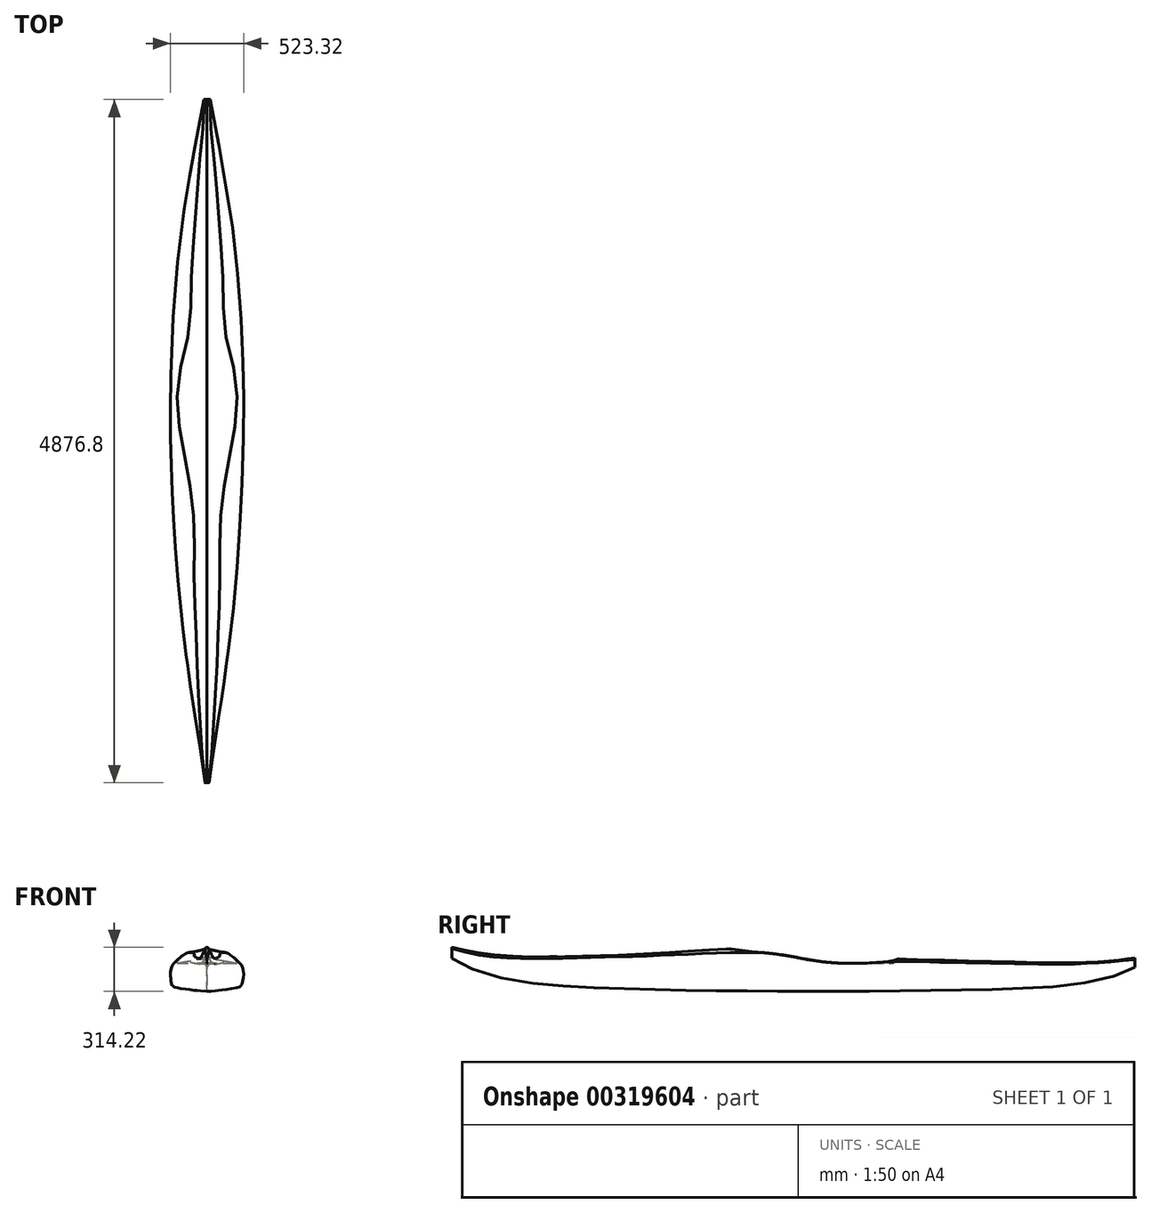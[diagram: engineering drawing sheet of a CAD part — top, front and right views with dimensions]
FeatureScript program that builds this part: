
annotation { "Feature Type Name" : "Feature", "Feature Type Description" : "" }
export const myFeature = defineFeature(function(context is Context, id is Id, definition is map)
    precondition{}
    {
        {
            var Q0;
            Q0=qCreatedBy(makeId("Front.planeOp"),FACE);
            var sketch = newSketch(context, id + "F0", { "sketchPlane" : qUnion([Q0])});
            skLineSegment(sketch, "E0", {"start": v(0, 0) * mm, "end": v(537.15, 0) * mm, "construction": true});
            skPoint(sketch, "E1", {"position": v(0, 0) * mm});
            skLineSegment(sketch, "E2.direction1", {"start": v(0, 0) * mm, "end": v(25.4, 0) * mm, "construction": true});
            skLineSegment(sketch, "E3", {"start": v(0, 0) * mm, "end": v(0, 215.9) * mm, "construction": true});
            skLineSegment(sketch, "E4", {"start": v(25.4, 0) * mm, "end": v(25.4, 210.06) * mm, "construction": true});
            skLineSegment(sketch, "E5", {"start": v(50.8, 0) * mm, "end": v(50.8, 203.7) * mm, "construction": true});
            skLineSegment(sketch, "E6", {"start": v(76.2, 0) * mm, "end": v(76.2, 197.1) * mm, "construction": true});
            skLineSegment(sketch, "E7", {"start": v(101.6, 0) * mm, "end": v(101.6, 190.25) * mm, "construction": true});
            skLineSegment(sketch, "E8", {"start": v(127, 0) * mm, "end": v(127, 181.86) * mm, "construction": true});
            skLineSegment(sketch, "E9", {"start": v(152.4, 0) * mm, "end": v(152.4, 170.43) * mm, "construction": true});
            skLineSegment(sketch, "E10", {"start": v(177.8, 0) * mm, "end": v(177.8, 155.7) * mm, "construction": true});
            skLineSegment(sketch, "E11", {"start": v(203.2, 0) * mm, "end": v(203.2, 136.9) * mm, "construction": true});
            skLineSegment(sketch, "E12", {"start": v(228.6, 0) * mm, "end": v(228.6, 108.97) * mm, "construction": true});
            skLineSegment(sketch, "E13", {"start": v(0, 0) * mm, "end": v(0, -82.55) * mm, "construction": true});
            skLineSegment(sketch, "E14", {"start": v(25.4, 0) * mm, "end": v(25.4, -79.76) * mm, "construction": true});
            skLineSegment(sketch, "E15", {"start": v(50.8, 0) * mm, "end": v(50.8, -76.7) * mm, "construction": true});
            skLineSegment(sketch, "E16", {"start": v(76.2, 0) * mm, "end": v(76.2, -73.15) * mm, "construction": true});
            skLineSegment(sketch, "E17", {"start": v(101.6, 0) * mm, "end": v(101.6, -69.34) * mm, "construction": true});
            skLineSegment(sketch, "E18", {"start": v(127, 0) * mm, "end": v(127, -65.02) * mm, "construction": true});
            skLineSegment(sketch, "E19", {"start": v(152.4, 0) * mm, "end": v(152.4, -59.44) * mm, "construction": true});
            skLineSegment(sketch, "E20", {"start": v(177.8, 0) * mm, "end": v(177.8, -53.09) * mm, "construction": true});
            skLineSegment(sketch, "E21", {"start": v(203.2, 0) * mm, "end": v(203.2, -43.43) * mm, "construction": true});
            skLineSegment(sketch, "E22", {"start": v(228.6, 0) * mm, "end": v(228.6, -24.13) * mm, "construction": true});
            skPoint(sketch, "E23.0.1.0", {"position": v(0, 25.4) * mm});
            skPoint(sketch, "E23.0.2.0", {"position": v(0, 50.8) * mm});
            skPoint(sketch, "E23.0.3.0", {"position": v(0, 76.2) * mm});
            skPoint(sketch, "E23.0.4.0", {"position": v(0, 101.6) * mm});
            skPoint(sketch, "E23.0.5.0", {"position": v(0, 127) * mm});
            skPoint(sketch, "E23.0.6.0", {"position": v(0, 152.4) * mm});
            skLineSegment(sketch, "E23.direction2", {"start": v(0, 0) * mm, "end": v(0, 25.4) * mm, "construction": true});
            skLineSegment(sketch, "E24", {"start": v(0, 25.4) * mm, "end": v(241.8, 25.4) * mm, "construction": true});
            skLineSegment(sketch, "E25", {"start": v(0, 50.8) * mm, "end": v(243.33, 50.8) * mm, "construction": true});
            skLineSegment(sketch, "E26", {"start": v(0, 76.2) * mm, "end": v(241.3, 76.2) * mm, "construction": true});
            skLineSegment(sketch, "E27", {"start": v(0, 101.6) * mm, "end": v(232.92, 101.6) * mm, "construction": true});
            skPoint(sketch, "E28", {"position": v(238, 0) * mm});
            skFitSpline(sketch, "E29", {"points": [v(0, 215.9) * mm, v(25.4, 210.06) * mm, v(50.8, 203.7) * mm, v(76.2, 197.1) * mm, v(101.6, 190.25) * mm, v(127, 181.86) * mm, v(152.4, 170.43) * mm, v(177.8, 155.7) * mm, v(203.2, 136.9) * mm, v(228.6, 108.97) * mm, v(241.3, 76.2) * mm, v(243.33, 50.8) * mm, v(241.8, 25.4) * mm, v(238, 0) * mm, v(228.6, -24.13) * mm, v(203.2, -43.43) * mm, v(177.8, -53.09) * mm, v(152.4, -59.44) * mm, v(127, -65.02) * mm, v(101.6, -69.34) * mm, v(76.2, -73.15) * mm, v(50.8, -76.7) * mm, v(25.4, -79.76) * mm, v(0, -82.55) * mm], "startDerivative": vector(600.69, -135.37) * mm, "endDerivative": vector(-606.38, -65.85) * mm});
            skFitSpline(sketch, "E30.MirrorCS", {"points": [v(0, 215.9) * mm, v(-25.4, 210.06) * mm, v(-50.8, 203.7) * mm, v(-76.2, 197.1) * mm, v(-101.6, 190.25) * mm, v(-127, 181.86) * mm, v(-152.4, 170.43) * mm, v(-177.8, 155.7) * mm, v(-203.2, 136.9) * mm, v(-228.6, 108.97) * mm, v(-241.3, 76.2) * mm, v(-243.33, 50.8) * mm, v(-241.8, 25.4) * mm, v(-238, 0) * mm, v(-228.6, -24.13) * mm, v(-203.2, -43.43) * mm, v(-177.8, -53.09) * mm, v(-152.4, -59.44) * mm, v(-127, -65.02) * mm, v(-101.6, -69.34) * mm, v(-76.2, -73.15) * mm, v(-50.8, -76.7) * mm, v(-25.4, -79.76) * mm, v(0, -82.55) * mm], "startDerivative": vector(-600.69, -135.37) * mm, "endDerivative": vector(606.38, -65.85) * mm});
            skPoint(sketch, "E31.0.0.7", {"position": v(0, 177.8) * mm});
            skPoint(sketch, "E32.0.0.8", {"position": v(0, 203.2) * mm});
            skPoint(sketch, "E33.0.1.0", {"position": v(25.4, 0) * mm});
            skPoint(sketch, "E33.0.2.0", {"position": v(50.8, 0) * mm});
            skPoint(sketch, "E33.0.3.0", {"position": v(76.2, 0) * mm});
            skPoint(sketch, "E33.0.4.0", {"position": v(101.6, 0) * mm});
            skPoint(sketch, "E33.0.5.0", {"position": v(127, 0) * mm});
            skPoint(sketch, "E33.0.6.0", {"position": v(152.4, 0) * mm});
            skPoint(sketch, "E33.0.7.0", {"position": v(177.8, 0) * mm});
            skPoint(sketch, "E33.0.8.0", {"position": v(203.2, 0) * mm});
            skPoint(sketch, "E33.0.9.0", {"position": v(228.6, 0) * mm});
            skPoint(sketch, "E34.0.10.0", {"position": v(254, 0) * mm});
            skPoint(sketch, "E35.0.11.0", {"position": v(279.4, 0) * mm});
            skPoint(sketch, "E36", {"position": v(0, -25.4) * mm});
            skPoint(sketch, "E37", {"position": v(0, -50.8) * mm});
            skPoint(sketch, "E38", {"position": v(0, -76.2) * mm});
            skLineSegment(sketch, "E39", {"start": v(0, -82.55) * mm, "end": v(0, 215.9) * mm});
            skLineSegment(sketch, "E40", {"start": v(0, 215.9) * mm, "end": v(0, -82.55) * mm});
            skSolve(sketch);
        }
        {
            var Q0;
            Q0=makeQuery(id+"F0.imprint","IMPRINT",FACE,{"disambiguationData":[TD([[makeQuery(id+"F0.imprint","IMPRINT",EDGE,{"derivedFrom":sQuery(id+"F0.wireOp",EDGE,"E29")}),-1.0]])]});
            cPlane(context, id + "F1", {"entities" : qUnion([Q0]), "cplaneType" : CPlaneType.OFFSET, "offset" : 304.8 * mm, "width" : 152.4 * mm, "height" : 152.4 * mm});
        }
        {
            var Q0;
            Q0=qCreatedBy(id+"F1.planeOp",FACE);
            var sketch = newSketch(context, id + "F2", { "sketchPlane" : qUnion([Q0])});
            skPoint(sketch, "E41.0", {"position": v(0, 0) * mm});
            skPoint(sketch, "E42.0", {"position": v(25.4, 0) * mm});
            skPoint(sketch, "E43.0", {"position": v(50.8, 0) * mm});
            skPoint(sketch, "E44.0", {"position": v(76.2, 0) * mm});
            skPoint(sketch, "E45.0", {"position": v(101.6, 0) * mm});
            skPoint(sketch, "E46.0", {"position": v(127, 0) * mm});
            skPoint(sketch, "E47.0", {"position": v(177.8, 0) * mm});
            skPoint(sketch, "E48.0", {"position": v(203.2, 0) * mm});
            skPoint(sketch, "E49.0", {"position": v(0, 25.4) * mm});
            skPoint(sketch, "E50.0", {"position": v(0, 50.8) * mm});
            skPoint(sketch, "E51.0", {"position": v(0, 76.2) * mm});
            skPoint(sketch, "E52.0", {"position": v(0, 101.6) * mm});
            skPoint(sketch, "E53.0", {"position": v(152.4, 0) * mm});
            skLineSegment(sketch, "E54", {"start": v(0, 0) * mm, "end": v(0, 198.12) * mm, "construction": true});
            skLineSegment(sketch, "E55", {"start": v(25.4, 0) * mm, "end": v(25.4, 192.53) * mm, "construction": true});
            skLineSegment(sketch, "E56", {"start": v(50.8, 0) * mm, "end": v(50.8, 187.2) * mm, "construction": true});
            skLineSegment(sketch, "E57", {"start": v(76.2, 0) * mm, "end": v(76.2, 181.61) * mm, "construction": true});
            skLineSegment(sketch, "E58", {"start": v(101.6, 0) * mm, "end": v(101.6, 175.51) * mm, "construction": true});
            skLineSegment(sketch, "E59", {"start": v(127, 0) * mm, "end": v(127, 167.9) * mm, "construction": true});
            skLineSegment(sketch, "E60", {"start": v(152.4, 0) * mm, "end": v(152.4, 157.23) * mm, "construction": true});
            skLineSegment(sketch, "E61", {"start": v(177.8, 0) * mm, "end": v(177.8, 142.75) * mm, "construction": true});
            skLineSegment(sketch, "E62", {"start": v(203.2, 0) * mm, "end": v(203.2, 120.65) * mm, "construction": true});
            skLineSegment(sketch, "E63", {"start": v(0, 0) * mm, "end": v(0, -78.23) * mm, "construction": true});
            skLineSegment(sketch, "E64", {"start": v(25.4, 0) * mm, "end": v(25.4, -73.91) * mm, "construction": true});
            skLineSegment(sketch, "E65", {"start": v(50.8, 0) * mm, "end": v(50.8, -69.34) * mm, "construction": true});
            skLineSegment(sketch, "E66", {"start": v(76.2, 0) * mm, "end": v(76.2, -64.52) * mm, "construction": true});
            skLineSegment(sketch, "E67", {"start": v(101.6, 0) * mm, "end": v(101.6, -58.93) * mm, "construction": true});
            skLineSegment(sketch, "E68", {"start": v(127, 0) * mm, "end": v(127, -52.83) * mm, "construction": true});
            skLineSegment(sketch, "E69", {"start": v(152.4, 0) * mm, "end": v(152.4, -45.72) * mm, "construction": true});
            skLineSegment(sketch, "E70", {"start": v(177.8, 0) * mm, "end": v(177.8, -36.32) * mm, "construction": true});
            skLineSegment(sketch, "E71", {"start": v(203.2, 0) * mm, "end": v(203.2, -20.83) * mm, "construction": true});
            skLineSegment(sketch, "E72", {"start": v(0, 25.4) * mm, "end": v(222.5, 25.4) * mm, "construction": true});
            skLineSegment(sketch, "E73", {"start": v(0, 50.8) * mm, "end": v(225.04, 50.8) * mm, "construction": true});
            skLineSegment(sketch, "E74", {"start": v(0, 0) * mm, "end": v(215.9, 0) * mm, "construction": true});
            skLineSegment(sketch, "E75", {"start": v(0, 76.2) * mm, "end": v(223.77, 76.2) * mm, "construction": true});
            skLineSegment(sketch, "E76", {"start": v(0, 101.6) * mm, "end": v(216.4, 101.6) * mm, "construction": true});
            skFitSpline(sketch, "E77", {"points": [v(0, 198.12) * mm, v(25.4, 192.53) * mm, v(50.8, 187.2) * mm, v(76.2, 181.61) * mm, v(101.6, 175.51) * mm, v(127, 167.9) * mm, v(152.4, 157.23) * mm, v(177.8, 142.75) * mm, v(203.2, 120.65) * mm, v(216.4, 101.6) * mm, v(223.77, 76.2) * mm, v(225.04, 50.8) * mm, v(222.5, 25.4) * mm, v(215.9, 0) * mm, v(203.2, -20.83) * mm, v(177.8, -36.32) * mm, v(152.4, -45.72) * mm, v(127, -52.83) * mm, v(101.6, -58.93) * mm, v(76.2, -64.52) * mm, v(50.8, -69.34) * mm, v(25.4, -73.91) * mm, v(0, -78.23) * mm], "startDerivative": vector(564.48, -125.99) * mm, "endDerivative": vector(-567.44, -95.07) * mm});
            skFitSpline(sketch, "E78.MirrorCS", {"points": [v(0, 198.12) * mm, v(-25.4, 192.53) * mm, v(-50.8, 187.2) * mm, v(-76.2, 181.61) * mm, v(-101.6, 175.51) * mm, v(-127, 167.9) * mm, v(-152.4, 157.23) * mm, v(-177.8, 142.75) * mm, v(-203.2, 120.65) * mm, v(-216.4, 101.6) * mm, v(-223.77, 76.2) * mm, v(-225.04, 50.8) * mm, v(-222.5, 25.4) * mm, v(-215.9, 0) * mm, v(-203.2, -20.83) * mm, v(-177.8, -36.32) * mm, v(-152.4, -45.72) * mm, v(-127, -52.83) * mm, v(-101.6, -58.93) * mm, v(-76.2, -64.52) * mm, v(-50.8, -69.34) * mm, v(-25.4, -73.91) * mm, v(0, -78.23) * mm], "startDerivative": vector(-564.48, -125.99) * mm, "endDerivative": vector(567.44, -95.07) * mm});
            skLineSegment(sketch, "E79", {"start": v(0, 198.12) * mm, "end": v(0, -78.23) * mm});
            skSolve(sketch);
        }
        {
            var Q0;
            Q0=makeQuery(id+"F2.imprint","IMPRINT",FACE,{"disambiguationData":[TD([[makeQuery(id+"F2.imprint","IMPRINT",EDGE,{"derivedFrom":sQuery(id+"F2.wireOp",EDGE,"E77")}),-1.0]])]});
            cPlane(context, id + "F3", {"entities" : qUnion([Q0]), "cplaneType" : CPlaneType.OFFSET, "offset" : 304.8 * mm, "width" : 152.4 * mm, "height" : 152.4 * mm});
        }
        {
            var Q0;
            Q0=qCreatedBy(id+"F3.planeOp",FACE);
            var sketch = newSketch(context, id + "F4", { "sketchPlane" : qUnion([Q0])});
            skPoint(sketch, "E80.0", {"position": v(0, 0) * mm});
            skPoint(sketch, "E81.0", {"position": v(25.4, 0) * mm});
            skPoint(sketch, "E82.0", {"position": v(50.8, 0) * mm});
            skPoint(sketch, "E83.0", {"position": v(76.2, 0) * mm});
            skPoint(sketch, "E84.0", {"position": v(101.6, 0) * mm});
            skPoint(sketch, "E85.0", {"position": v(127, 0) * mm});
            skPoint(sketch, "E86.0", {"position": v(152.4, 0) * mm});
            skPoint(sketch, "E87.0", {"position": v(177.8, 0) * mm});
            skPoint(sketch, "E88.0", {"position": v(0, 25.4) * mm});
            skPoint(sketch, "E89.0", {"position": v(0, 50.8) * mm});
            skPoint(sketch, "E90.0", {"position": v(0, 76.2) * mm});
            skPoint(sketch, "E91.0", {"position": v(0, 101.6) * mm});
            skLineSegment(sketch, "E92", {"start": v(0, 0) * mm, "end": v(0, 181.36) * mm, "construction": true});
            skLineSegment(sketch, "E93", {"start": v(25.4, 0) * mm, "end": v(25.4, 177.3) * mm, "construction": true});
            skLineSegment(sketch, "E94", {"start": v(50.8, 0) * mm, "end": v(50.8, 172.97) * mm, "construction": true});
            skLineSegment(sketch, "E95", {"start": v(76.2, 0) * mm, "end": v(76.2, 168.66) * mm, "construction": true});
            skLineSegment(sketch, "E96", {"start": v(101.6, 0) * mm, "end": v(101.6, 163.07) * mm, "construction": true});
            skLineSegment(sketch, "E97", {"start": v(127, 0) * mm, "end": v(127, 154.94) * mm, "construction": true});
            skLineSegment(sketch, "E98", {"start": v(152.4, 0) * mm, "end": v(152.4, 142.5) * mm, "construction": true});
            skLineSegment(sketch, "E99", {"start": v(177.8, 0) * mm, "end": v(177.8, 123.2) * mm, "construction": true});
            skLineSegment(sketch, "E100", {"start": v(0, 0) * mm, "end": v(0, -72.14) * mm, "construction": true});
            skLineSegment(sketch, "E101", {"start": v(25.4, 0) * mm, "end": v(25.4, -65.02) * mm, "construction": true});
            skLineSegment(sketch, "E102", {"start": v(50.8, 0) * mm, "end": v(50.8, -58.17) * mm, "construction": true});
            skLineSegment(sketch, "E103", {"start": v(76.2, 0) * mm, "end": v(76.2, -50.8) * mm, "construction": true});
            skLineSegment(sketch, "E104", {"start": v(101.6, 0) * mm, "end": v(101.6, -42.93) * mm, "construction": true});
            skLineSegment(sketch, "E105", {"start": v(127, 0) * mm, "end": v(127, -34.04) * mm, "construction": true});
            skLineSegment(sketch, "E106", {"start": v(152.4, 0) * mm, "end": v(152.4, -23.37) * mm, "construction": true});
            skLineSegment(sketch, "E107", {"start": v(177.8, 0) * mm, "end": v(177.8, -7.37) * mm, "construction": true});
            skLineSegment(sketch, "E108", {"start": v(0, 0) * mm, "end": v(184.66, 0) * mm, "construction": true});
            skLineSegment(sketch, "E109", {"start": v(0, 25.4) * mm, "end": v(195.58, 25.4) * mm, "construction": true});
            skLineSegment(sketch, "E110", {"start": v(0, 50.8) * mm, "end": v(200.15, 50.8) * mm, "construction": true});
            skLineSegment(sketch, "E111", {"start": v(0, 76.2) * mm, "end": v(199.9, 76.2) * mm, "construction": true});
            skLineSegment(sketch, "E112", {"start": v(0, 101.6) * mm, "end": v(193.3, 101.6) * mm, "construction": true});
            skFitSpline(sketch, "E113", {"points": [v(0, 181.36) * mm, v(25.4, 177.3) * mm, v(50.8, 172.97) * mm, v(76.2, 168.66) * mm, v(101.6, 163.07) * mm, v(127, 154.94) * mm, v(152.4, 142.5) * mm, v(177.8, 123.2) * mm, v(193.3, 101.6) * mm, v(199.9, 76.2) * mm, v(200.15, 50.8) * mm, v(195.58, 25.4) * mm, v(184.66, 0) * mm, v(177.8, -7.37) * mm, v(152.4, -23.37) * mm, v(127, -34.04) * mm, v(101.6, -42.93) * mm, v(76.2, -50.8) * mm, v(50.8, -58.17) * mm, v(25.4, -65.02) * mm, v(0, -72.14) * mm], "startDerivative": vector(509.78, -79.9) * mm, "endDerivative": vector(-503.06, -142.83) * mm});
            skFitSpline(sketch, "E114.MirrorCS", {"points": [v(0, 181.36) * mm, v(-25.4, 177.3) * mm, v(-50.8, 172.97) * mm, v(-76.2, 168.66) * mm, v(-101.6, 163.07) * mm, v(-127, 154.94) * mm, v(-152.4, 142.5) * mm, v(-177.8, 123.2) * mm, v(-193.3, 101.6) * mm, v(-199.9, 76.2) * mm, v(-200.15, 50.8) * mm, v(-195.58, 25.4) * mm, v(-184.66, 0) * mm, v(-177.8, -7.37) * mm, v(-152.4, -23.37) * mm, v(-127, -34.04) * mm, v(-101.6, -42.93) * mm, v(-76.2, -50.8) * mm, v(-50.8, -58.17) * mm, v(-25.4, -65.02) * mm, v(0, -72.14) * mm], "startDerivative": vector(-509.78, -79.9) * mm, "endDerivative": vector(503.06, -142.83) * mm});
            skLineSegment(sketch, "E115", {"start": v(0, 181.36) * mm, "end": v(0, -72.14) * mm});
            skSolve(sketch);
        }
        {
            var Q0;
            Q0=makeQuery(id+"F4.imprint","IMPRINT",FACE,{"disambiguationData":[TD([[makeQuery(id+"F4.imprint","IMPRINT",EDGE,{"derivedFrom":sQuery(id+"F4.wireOp",EDGE,"E113")}),-1.0]])]});
            cPlane(context, id + "F5", {"entities" : qUnion([Q0]), "cplaneType" : CPlaneType.OFFSET, "offset" : 304.8 * mm, "width" : 152.4 * mm, "height" : 152.4 * mm});
        }
        {
            var Q0;
            Q0=qCreatedBy(id+"F5.planeOp",FACE);
            var sketch = newSketch(context, id + "F6", { "sketchPlane" : qUnion([Q0])});
            skPoint(sketch, "E116.0", {"position": v(0, 0) * mm});
            skPoint(sketch, "E117.0", {"position": v(25.4, 0) * mm});
            skPoint(sketch, "E118.0", {"position": v(50.8, 0) * mm});
            skPoint(sketch, "E119.0", {"position": v(76.2, 0) * mm});
            skPoint(sketch, "E120.0", {"position": v(101.6, 0) * mm});
            skPoint(sketch, "E121.0", {"position": v(127, 0) * mm});
            skPoint(sketch, "E122.0", {"position": v(152.4, 0) * mm});
            skPoint(sketch, "E123.0", {"position": v(0, 25.4) * mm});
            skPoint(sketch, "E124.0", {"position": v(0, 50.8) * mm});
            skPoint(sketch, "E125.0", {"position": v(0, 76.2) * mm});
            skPoint(sketch, "E126.0", {"position": v(0, 101.6) * mm});
            skPoint(sketch, "E127.0", {"position": v(0, 127) * mm});
            skPoint(sketch, "E128.0", {"position": v(0, 152.4) * mm});
            skLineSegment(sketch, "E129", {"start": v(0, 0) * mm, "end": v(0, 168.15) * mm, "construction": true});
            skLineSegment(sketch, "E130", {"start": v(25.4, 0) * mm, "end": v(25.4, 165.6) * mm, "construction": true});
            skLineSegment(sketch, "E131", {"start": v(50.8, 0) * mm, "end": v(50.8, 162.3) * mm, "construction": true});
            skLineSegment(sketch, "E132", {"start": v(76.2, 0) * mm, "end": v(76.2, 157.99) * mm, "construction": true});
            skLineSegment(sketch, "E133", {"start": v(101.6, 0) * mm, "end": v(101.6, 150.62) * mm, "construction": true});
            skLineSegment(sketch, "E134", {"start": v(127, 0) * mm, "end": v(127, 138.68) * mm, "construction": true});
            skLineSegment(sketch, "E135", {"start": v(152.4, 0) * mm, "end": v(152.4, 118.11) * mm, "construction": true});
            skLineSegment(sketch, "E136", {"start": v(0, 0) * mm, "end": v(0, -61.47) * mm, "construction": true});
            skLineSegment(sketch, "E137", {"start": v(25.4, 0) * mm, "end": v(25.4, -50.3) * mm, "construction": true});
            skLineSegment(sketch, "E138", {"start": v(50.8, 0) * mm, "end": v(50.8, -40.13) * mm, "construction": true});
            skLineSegment(sketch, "E139", {"start": v(76.2, 0) * mm, "end": v(76.2, -29.46) * mm, "construction": true});
            skLineSegment(sketch, "E140", {"start": v(101.6, 0) * mm, "end": v(101.6, -18.03) * mm, "construction": true});
            skLineSegment(sketch, "E141", {"start": v(127, 0) * mm, "end": v(127, -4.57) * mm, "construction": true});
            skLineSegment(sketch, "E142", {"start": v(0, 0) * mm, "end": v(134.37, 0) * mm, "construction": true});
            skLineSegment(sketch, "E143", {"start": v(0, 25.4) * mm, "end": v(158.5, 25.4) * mm, "construction": true});
            skLineSegment(sketch, "E144", {"start": v(0, 50.8) * mm, "end": v(166.62, 50.8) * mm, "construction": true});
            skLineSegment(sketch, "E145", {"start": v(0, 76.2) * mm, "end": v(168.4, 76.2) * mm, "construction": true});
            skLineSegment(sketch, "E146", {"start": v(0, 101.6) * mm, "end": v(162.56, 101.6) * mm, "construction": true});
            skPoint(sketch, "E147", {"position": v(152.4, 15.5) * mm});
            skFitSpline(sketch, "E148", {"points": [v(0, 168.15) * mm, v(25.4, 165.6) * mm, v(50.8, 162.3) * mm, v(76.2, 157.99) * mm, v(101.6, 150.62) * mm, v(127, 138.68) * mm, v(152.4, 118.11) * mm, v(162.56, 101.6) * mm, v(168.4, 76.2) * mm, v(166.62, 50.8) * mm, v(158.5, 25.4) * mm, v(152.4, 15.5) * mm, v(134.37, 0) * mm, v(127, -4.57) * mm, v(101.6, -18.03) * mm, v(76.2, -29.46) * mm, v(50.8, -40.13) * mm, v(25.4, -50.3) * mm, v(0, -61.47) * mm], "startDerivative": vector(445.96, -41.5) * mm, "endDerivative": vector(-427.08, -193.13) * mm});
            skFitSpline(sketch, "E149.MirrorCS", {"points": [v(0, 168.15) * mm, v(-25.4, 165.6) * mm, v(-50.8, 162.3) * mm, v(-76.2, 157.99) * mm, v(-101.6, 150.62) * mm, v(-127, 138.68) * mm, v(-152.4, 118.11) * mm, v(-162.56, 101.6) * mm, v(-168.4, 76.2) * mm, v(-166.62, 50.8) * mm, v(-158.5, 25.4) * mm, v(-152.4, 15.5) * mm, v(-134.37, 0) * mm, v(-127, -4.57) * mm, v(-101.6, -18.03) * mm, v(-76.2, -29.46) * mm, v(-50.8, -40.13) * mm, v(-25.4, -50.3) * mm, v(0, -61.47) * mm], "startDerivative": vector(-445.96, -41.5) * mm, "endDerivative": vector(427.08, -193.13) * mm});
            skLineSegment(sketch, "E150", {"start": v(0, 168.15) * mm, "end": v(0, -61.47) * mm});
            skSolve(sketch);
        }
        {
            var Q0;
            Q0=makeQuery(id+"F6.imprint","IMPRINT",FACE,{"disambiguationData":[TD([[makeQuery(id+"F6.imprint","IMPRINT",EDGE,{"derivedFrom":sQuery(id+"F6.wireOp",EDGE,"E148")}),-1.0]])]});
            cPlane(context, id + "F7", {"entities" : qUnion([Q0]), "cplaneType" : CPlaneType.OFFSET, "offset" : 304.8 * mm, "width" : 152.4 * mm, "height" : 152.4 * mm});
        }
        {
            var Q0;
            Q0=qCreatedBy(id+"F7.planeOp",FACE);
            var sketch = newSketch(context, id + "F8", { "sketchPlane" : qUnion([Q0])});
            skPoint(sketch, "E151.0", {"position": v(0, 0) * mm});
            skPoint(sketch, "E152.0", {"position": v(25.4, 0) * mm});
            skPoint(sketch, "E153.0", {"position": v(50.8, 0) * mm});
            skPoint(sketch, "E154.0", {"position": v(76.2, 0) * mm});
            skPoint(sketch, "E155.0", {"position": v(101.6, 0) * mm});
            skPoint(sketch, "E156.0", {"position": v(127, 0) * mm});
            skPoint(sketch, "E157.0", {"position": v(0, 25.4) * mm});
            skPoint(sketch, "E158.0", {"position": v(0, 50.8) * mm});
            skPoint(sketch, "E159.0", {"position": v(0, 76.2) * mm});
            skPoint(sketch, "E160.0", {"position": v(0, 101.6) * mm});
            skLineSegment(sketch, "E161", {"start": v(0, 0) * mm, "end": v(0, 161.3) * mm, "construction": true});
            skLineSegment(sketch, "E162", {"start": v(25.4, 0) * mm, "end": v(25.4, 159.51) * mm, "construction": true});
            skLineSegment(sketch, "E163", {"start": v(50.8, 0) * mm, "end": v(50.8, 155.2) * mm, "construction": true});
            skLineSegment(sketch, "E164", {"start": v(76.2, 0) * mm, "end": v(76.2, 147.07) * mm, "construction": true});
            skLineSegment(sketch, "E165", {"start": v(101.6, 0) * mm, "end": v(101.6, 132.84) * mm, "construction": true});
            skLineSegment(sketch, "E166", {"start": v(127, 0) * mm, "end": v(127, 96.27) * mm, "construction": true});
            skLineSegment(sketch, "E167", {"start": v(0, 0) * mm, "end": v(0, -44.2) * mm, "construction": true});
            skLineSegment(sketch, "E168", {"start": v(25.4, 0) * mm, "end": v(25.4, -27.43) * mm, "construction": true});
            skLineSegment(sketch, "E169", {"start": v(50.8, 0) * mm, "end": v(50.8, -12.45) * mm, "construction": true});
            skLineSegment(sketch, "E170", {"start": v(76.2, 0) * mm, "end": v(76.2, 3.81) * mm, "construction": true});
            skLineSegment(sketch, "E171", {"start": v(101.6, 0) * mm, "end": v(101.6, 22.35) * mm, "construction": true});
            skLineSegment(sketch, "E172", {"start": v(127, 0) * mm, "end": v(127, 65.02) * mm, "construction": true});
            skLineSegment(sketch, "E173", {"start": v(0, 76.2) * mm, "end": v(128.52, 76.2) * mm, "construction": true});
            skLineSegment(sketch, "E174", {"start": v(0, 50.8) * mm, "end": v(122.94, 50.8) * mm, "construction": true});
            skLineSegment(sketch, "E175", {"start": v(0, 25.4) * mm, "end": v(104.9, 25.4) * mm, "construction": true});
            skLineSegment(sketch, "E176", {"start": v(0, 0) * mm, "end": v(70.36, 0) * mm, "construction": true});
            skPoint(sketch, "E177", {"position": v(0, -25.4) * mm});
            skFitSpline(sketch, "E178", {"points": [v(0, 161.3) * mm, v(25.4, 159.51) * mm, v(50.8, 155.2) * mm, v(76.2, 147.07) * mm, v(101.6, 132.84) * mm, v(127, 96.27) * mm, v(128.52, 76.2) * mm, v(127, 65.02) * mm, v(122.94, 50.8) * mm, v(104.9, 25.4) * mm, v(101.6, 22.35) * mm, v(76.2, 3.81) * mm, v(70.36, 0) * mm, v(50.8, -12.45) * mm, v(25.4, -27.43) * mm, v(0, -44.2) * mm], "startDerivative": vector(393.47, -0.46) * mm, "endDerivative": vector(-325.6, -222.45) * mm});
            skFitSpline(sketch, "E179.MirrorCS", {"points": [v(0, 161.3) * mm, v(-25.4, 159.51) * mm, v(-50.8, 155.2) * mm, v(-76.2, 147.07) * mm, v(-101.6, 132.84) * mm, v(-127, 96.27) * mm, v(-128.52, 76.2) * mm, v(-127, 65.02) * mm, v(-122.94, 50.8) * mm, v(-104.9, 25.4) * mm, v(-101.6, 22.35) * mm, v(-76.2, 3.81) * mm, v(-70.36, 0) * mm, v(-50.8, -12.45) * mm, v(-25.4, -27.43) * mm, v(0, -44.2) * mm], "startDerivative": vector(-393.47, -0.46) * mm, "endDerivative": vector(325.6, -222.45) * mm});
            skLineSegment(sketch, "E180", {"start": v(0, 161.3) * mm, "end": v(0, -44.2) * mm});
            skSolve(sketch);
        }
        {
            var Q0;
            Q0=makeQuery(id+"F8.imprint","IMPRINT",FACE,{"disambiguationData":[TD([[makeQuery(id+"F8.imprint","IMPRINT",EDGE,{"derivedFrom":sQuery(id+"F8.wireOp",EDGE,"E178")}),-1.0]])]});
            cPlane(context, id + "F9", {"entities" : qUnion([Q0]), "cplaneType" : CPlaneType.OFFSET, "offset" : 304.8 * mm, "width" : 152.4 * mm, "height" : 152.4 * mm});
        }
        {
            var Q0;
            Q0=qCreatedBy(id+"F9.planeOp",FACE);
            var sketch = newSketch(context, id + "F10", { "sketchPlane" : qUnion([Q0])});
            skPoint(sketch, "E181.0", {"position": v(0, 0) * mm});
            skPoint(sketch, "E182.0", {"position": v(25.4, 0) * mm});
            skPoint(sketch, "E183.0", {"position": v(50.8, 0) * mm});
            skPoint(sketch, "E184.0", {"position": v(76.2, 0) * mm});
            skPoint(sketch, "E185.0", {"position": v(0, 25.4) * mm});
            skPoint(sketch, "E186.0", {"position": v(0, 50.8) * mm});
            skPoint(sketch, "E187.0", {"position": v(0, 76.2) * mm});
            skPoint(sketch, "E188.0", {"position": v(0, 101.6) * mm});
            skPoint(sketch, "E189.0", {"position": v(0, 127) * mm});
            skPoint(sketch, "E190.0", {"position": v(0, 152.4) * mm});
            skLineSegment(sketch, "E191", {"start": v(0, 0) * mm, "end": v(0, 163.58) * mm, "construction": true});
            skLineSegment(sketch, "E192", {"start": v(25.4, 0) * mm, "end": v(25.4, 160.27) * mm, "construction": true});
            skLineSegment(sketch, "E193", {"start": v(50.8, 0) * mm, "end": v(50.8, 148.84) * mm, "construction": true});
            skLineSegment(sketch, "E194", {"start": v(76.2, 0) * mm, "end": v(76.2, 123.95) * mm, "construction": true});
            skLineSegment(sketch, "E195", {"start": v(0, 0) * mm, "end": v(0, -10.41) * mm, "construction": true});
            skLineSegment(sketch, "E196", {"start": v(25.4, 0) * mm, "end": v(25.4, 12.95) * mm, "construction": true});
            skLineSegment(sketch, "E197", {"start": v(50.8, 0) * mm, "end": v(50.8, 39.62) * mm, "construction": true});
            skLineSegment(sketch, "E198", {"start": v(76.2, 0) * mm, "end": v(76.2, 73.91) * mm, "construction": true});
            skLineSegment(sketch, "E199", {"start": v(0, 101.6) * mm, "end": v(81.79, 101.6) * mm, "construction": true});
            skLineSegment(sketch, "E200", {"start": v(0, 76.2) * mm, "end": v(77.22, 76.2) * mm, "construction": true});
            skLineSegment(sketch, "E201", {"start": v(0, 50.8) * mm, "end": v(60.96, 50.8) * mm, "construction": true});
            skLineSegment(sketch, "E202", {"start": v(0, 25.4) * mm, "end": v(37.85, 25.4) * mm, "construction": true});
            skLineSegment(sketch, "E203", {"start": v(0, 0) * mm, "end": v(12.2, 0) * mm, "construction": true});
            skLineSegment(sketch, "E204", {"start": v(0, 152.4) * mm, "end": v(44.96, 152.4) * mm, "construction": true});
            skFitSpline(sketch, "E205", {"points": [v(0, 163.58) * mm, v(25.4, 160.27) * mm, v(44.96, 152.4) * mm, v(50.8, 148.84) * mm, v(76.2, 123.95) * mm, v(81.79, 101.6) * mm, v(77.22, 76.2) * mm, v(60.96, 50.8) * mm, v(50.8, 39.62) * mm, v(37.85, 25.4) * mm, v(25.4, 12.95) * mm, v(12.2, 0) * mm, v(0, -10.41) * mm], "startDerivative": vector(320.67, -11.88) * mm, "endDerivative": vector(-169.53, -138.95) * mm});
            skFitSpline(sketch, "E206.MirrorCS", {"points": [v(0, 163.58) * mm, v(-25.4, 160.27) * mm, v(-44.96, 152.4) * mm, v(-50.8, 148.84) * mm, v(-76.2, 123.95) * mm, v(-81.79, 101.6) * mm, v(-77.22, 76.2) * mm, v(-60.96, 50.8) * mm, v(-50.8, 39.62) * mm, v(-37.85, 25.4) * mm, v(-25.4, 12.95) * mm, v(-12.2, 0) * mm, v(0, -10.41) * mm], "startDerivative": vector(-320.67, -11.88) * mm, "endDerivative": vector(169.53, -138.95) * mm});
            skLineSegment(sketch, "E207", {"start": v(0, 163.58) * mm, "end": v(0, -10.41) * mm});
            skSolve(sketch);
        }
        {
            var Q0;
            Q0=makeQuery(id+"F10.imprint","IMPRINT",FACE,{"disambiguationData":[TD([[makeQuery(id+"F10.imprint","IMPRINT",EDGE,{"derivedFrom":sQuery(id+"F10.wireOp",EDGE,"E205")}),-1.0]])]});
            cPlane(context, id + "F11", {"entities" : qUnion([Q0]), "cplaneType" : CPlaneType.OFFSET, "offset" : 304.8 * mm, "width" : 152.4 * mm, "height" : 152.4 * mm});
        }
        {
            var Q0;
            Q0=qCreatedBy(id+"F11.planeOp",FACE);
            var sketch = newSketch(context, id + "F12", { "sketchPlane" : qUnion([Q0])});
            skPoint(sketch, "E208.0", {"position": v(0, 0) * mm});
            skPoint(sketch, "E209.0", {"position": v(25.4, 0) * mm});
            skPoint(sketch, "E210.0", {"position": v(0, 25.4) * mm});
            skPoint(sketch, "E211.0", {"position": v(0, 50.8) * mm});
            skPoint(sketch, "E212.0", {"position": v(0, 76.2) * mm});
            skPoint(sketch, "E213.0", {"position": v(0, 101.6) * mm});
            skPoint(sketch, "E214.0", {"position": v(0, 127) * mm});
            skPoint(sketch, "E215.0", {"position": v(0, 152.4) * mm});
            skLineSegment(sketch, "E216", {"start": v(0, 0) * mm, "end": v(0, 195.07) * mm, "construction": true});
            skLineSegment(sketch, "E217", {"start": v(0, 0) * mm, "end": v(0, 70.61) * mm, "construction": true});
            skLineSegment(sketch, "E218", {"start": v(25.4, 0) * mm, "end": v(25.4, 121.16) * mm, "construction": true});
            skLineSegment(sketch, "E219", {"start": v(0, 76.2) * mm, "end": v(4.32, 76.2) * mm, "construction": true});
            skLineSegment(sketch, "E220", {"start": v(0, 101.6) * mm, "end": v(16, 101.6) * mm, "construction": true});
            skLineSegment(sketch, "E221", {"start": v(0, 127) * mm, "end": v(27.94, 127) * mm, "construction": true});
            skLineSegment(sketch, "E222", {"start": v(0, 152.4) * mm, "end": v(35.3, 152.4) * mm, "construction": true});
            skPoint(sketch, "E223.0", {"position": v(0, 177.8) * mm});
            skLineSegment(sketch, "E224", {"start": v(0, 177.8) * mm, "end": v(32, 177.8) * mm, "construction": true});
            skFitSpline(sketch, "E225", {"points": [v(0, 195.07) * mm, v(32, 177.8) * mm, v(35.3, 152.4) * mm, v(27.94, 127) * mm, v(25.4, 121.16) * mm, v(16, 101.6) * mm, v(4.32, 76.2) * mm, v(0, 70.61) * mm], "startDerivative": vector(319, -20.9) * mm, "endDerivative": vector(-51.4, -54.26) * mm});
            skFitSpline(sketch, "E226.MirrorCS", {"points": [v(0, 195.07) * mm, v(-32, 177.8) * mm, v(-35.3, 152.4) * mm, v(-27.94, 127) * mm, v(-25.4, 121.16) * mm, v(-16, 101.6) * mm, v(-4.32, 76.2) * mm, v(0, 70.61) * mm], "startDerivative": vector(-319, -20.9) * mm, "endDerivative": vector(51.4, -54.26) * mm});
            skLineSegment(sketch, "E227", {"start": v(0, 195.07) * mm, "end": v(0, 70.61) * mm});
            skSolve(sketch);
        }
        {
            var Q0;
            Q0=makeQuery(id+"F12.imprint","IMPRINT",FACE,{"disambiguationData":[TD([[makeQuery(id+"F12.imprint","IMPRINT",EDGE,{"derivedFrom":sQuery(id+"F12.wireOp",EDGE,"E225")}),-1.0]])]});
            cPlane(context, id + "F13", {"entities" : qUnion([Q0]), "cplaneType" : CPlaneType.OFFSET, "offset" : 152.4 * mm, "width" : 152.4 * mm, "height" : 152.4 * mm});
        }
        {
            var Q0;
            Q0=qCreatedBy(id+"F13.planeOp",FACE);
            var sketch = newSketch(context, id + "F14", { "sketchPlane" : qUnion([Q0])});
            skPoint(sketch, "E228.0", {"position": v(0, 0) * mm});
            skPoint(sketch, "E229.0", {"position": v(0, 25.4) * mm});
            skPoint(sketch, "E230.0", {"position": v(0, 50.8) * mm});
            skPoint(sketch, "E231.0", {"position": v(0, 76.2) * mm});
            skPoint(sketch, "E232.0", {"position": v(0, 101.6) * mm});
            skPoint(sketch, "E233.0", {"position": v(0, 127) * mm});
            skPoint(sketch, "E234.0", {"position": v(0, 152.4) * mm});
            skPoint(sketch, "E235.0", {"position": v(0, 177.8) * mm});
            skLineSegment(sketch, "E236", {"start": v(0, 0) * mm, "end": v(0, 227.33) * mm, "construction": true});
            skLineSegment(sketch, "E237", {"start": v(0, 0) * mm, "end": v(0, 148.6) * mm, "construction": true});
            skLineSegment(sketch, "E238", {"start": v(0, 152.4) * mm, "end": v(1.27, 152.4) * mm, "construction": true});
            skLineSegment(sketch, "E239", {"start": v(0, 177.8) * mm, "end": v(9.4, 177.8) * mm, "construction": true});
            skPoint(sketch, "E240.0", {"position": v(0, 203.2) * mm});
            skLineSegment(sketch, "E241", {"start": v(0, 203.2) * mm, "end": v(14.48, 203.2) * mm, "construction": true});
            skFitSpline(sketch, "E242", {"points": [v(0, 227.33) * mm, v(14.48, 203.2) * mm, v(9.4, 177.8) * mm, v(1.27, 152.4) * mm, v(0, 148.6) * mm], "startDerivative": vector(151.44, -12.56) * mm, "endDerivative": vector(-8.82, -25.32) * mm});
            skFitSpline(sketch, "E243.MirrorCS", {"points": [v(0, 227.33) * mm, v(-14.48, 203.2) * mm, v(-9.4, 177.8) * mm, v(-1.27, 152.4) * mm, v(0, 148.6) * mm], "startDerivative": vector(-151.44, -12.56) * mm, "endDerivative": vector(8.82, -25.32) * mm});
            skLineSegment(sketch, "E244", {"start": v(0, 227.33) * mm, "end": v(0, 148.6) * mm});
            skSolve(sketch);
        }
        {
            var Q0;
            Q0=makeQuery(id+"F0.imprint","IMPRINT",FACE,{"disambiguationData":[TD([[makeQuery(id+"F0.imprint","IMPRINT",EDGE,{"derivedFrom":sQuery(id+"F0.wireOp",EDGE,"E29")}),-1.0]])]});
            cPlane(context, id + "F15", {"entities" : qUnion([Q0]), "cplaneType" : CPlaneType.OFFSET, "offset" : 304.8 * mm, "oppositeDirection" : true, "width" : 152.4 * mm, "height" : 152.4 * mm});
        }
        {
            var Q0;
            Q0=qCreatedBy(id+"F15.planeOp",FACE);
            var sketch = newSketch(context, id + "F16", { "sketchPlane" : qUnion([Q0])});
            skPoint(sketch, "E245.0", {"position": v(0, 0) * mm});
            skPoint(sketch, "E246.0", {"position": v(25.4, 0) * mm});
            skPoint(sketch, "E247.0", {"position": v(50.8, 0) * mm});
            skPoint(sketch, "E248.0", {"position": v(76.2, 0) * mm});
            skPoint(sketch, "E249.0", {"position": v(101.6, 0) * mm});
            skPoint(sketch, "E250.0", {"position": v(127, 0) * mm});
            skPoint(sketch, "E251.0", {"position": v(152.4, 0) * mm});
            skPoint(sketch, "E252.0", {"position": v(177.8, 0) * mm});
            skPoint(sketch, "E253.0", {"position": v(203.2, 0) * mm});
            skPoint(sketch, "E254.0", {"position": v(228.6, 0) * mm});
            skPoint(sketch, "E255.0", {"position": v(0, 25.4) * mm});
            skPoint(sketch, "E256.0", {"position": v(0, 50.8) * mm});
            skPoint(sketch, "E257.0", {"position": v(0, 76.2) * mm});
            skPoint(sketch, "E258.0", {"position": v(0, 101.6) * mm});
            skPoint(sketch, "E259.0", {"position": v(0, 127) * mm});
            skPoint(sketch, "E260.0", {"position": v(254, 0) * mm});
            skLineSegment(sketch, "E261", {"start": v(0, 0) * mm, "end": v(0, -85.6) * mm, "construction": true});
            skLineSegment(sketch, "E262", {"start": v(25.4, 0) * mm, "end": v(25.4, -83.57) * mm, "construction": true});
            skLineSegment(sketch, "E263", {"start": v(50.8, 0) * mm, "end": v(50.8, -81.03) * mm, "construction": true});
            skLineSegment(sketch, "E264", {"start": v(76.2, 0) * mm, "end": v(76.2, -78.49) * mm, "construction": true});
            skLineSegment(sketch, "E265", {"start": v(101.6, 0) * mm, "end": v(101.6, -74.93) * mm, "construction": true});
            skLineSegment(sketch, "E266", {"start": v(127, 0) * mm, "end": v(127, -71.37) * mm, "construction": true});
            skLineSegment(sketch, "E267", {"start": v(152.4, 0) * mm, "end": v(152.4, -67.31) * mm, "construction": true});
            skLineSegment(sketch, "E268", {"start": v(177.8, 0) * mm, "end": v(177.8, -62.74) * mm, "construction": true});
            skLineSegment(sketch, "E269", {"start": v(203.2, 0) * mm, "end": v(203.2, -56.13) * mm, "construction": true});
            skLineSegment(sketch, "E270", {"start": v(228.6, 0) * mm, "end": v(228.6, -44.96) * mm, "construction": true});
            skLineSegment(sketch, "E271", {"start": v(254, 0) * mm, "end": v(254, 18.29) * mm, "construction": true});
            skLineSegment(sketch, "E272", {"start": v(254, 0) * mm, "end": v(254, 71.12) * mm, "construction": true});
            skPoint(sketch, "E272.endSnap0", {"position": v(254, 9.14) * mm});
            skLineSegment(sketch, "E273", {"start": v(228.6, 0) * mm, "end": v(228.6, 122.17) * mm, "construction": true});
            skLineSegment(sketch, "E274", {"start": v(203.2, 0) * mm, "end": v(203.2, 145.54) * mm, "construction": true});
            skLineSegment(sketch, "E275", {"start": v(177.8, 0) * mm, "end": v(177.8, 165.6) * mm, "construction": true});
            skLineSegment(sketch, "E276", {"start": v(152.4, 0) * mm, "end": v(152.4, 183.39) * mm, "construction": true});
            skPoint(sketch, "E277.0", {"position": v(0, -25.4) * mm});
            skPoint(sketch, "E278.0", {"position": v(0, -50.8) * mm});
            skPoint(sketch, "E279.0", {"position": v(0, -76.2) * mm});
            skPoint(sketch, "E280.0", {"position": v(0, 177.8) * mm});
            skPoint(sketch, "E281.0", {"position": v(0, 152.4) * mm});
            skLineSegment(sketch, "E282", {"start": v(0, 0) * mm, "end": v(251.2, 0) * mm, "construction": true});
            skLineSegment(sketch, "E283", {"start": v(0, -25.4) * mm, "end": v(245.35, -22.48) * mm, "construction": true});
            skPoint(sketch, "E283.endSnap0", {"position": v(228.6, -22.48) * mm});
            skLineSegment(sketch, "E284", {"start": v(0, -50.8) * mm, "end": v(217.68, -50.8) * mm, "construction": true});
            skLineSegment(sketch, "E285", {"start": v(0, 25.4) * mm, "end": v(254.76, 25.4) * mm, "construction": true});
            skLineSegment(sketch, "E286", {"start": v(0, 50.8) * mm, "end": v(255.78, 50.8) * mm, "construction": true});
            skLineSegment(sketch, "E287", {"start": v(0, 76.2) * mm, "end": v(252.98, 76.2) * mm, "construction": true});
            skLineSegment(sketch, "E288", {"start": v(0, 101.6) * mm, "end": v(243.59, 101.6) * mm, "construction": true});
            skLineSegment(sketch, "E289", {"start": v(0, 127) * mm, "end": v(224.03, 127) * mm, "construction": true});
            skLineSegment(sketch, "E290", {"start": v(0, 152.4) * mm, "end": v(194.56, 152.4) * mm, "construction": true});
            skLineSegment(sketch, "E291", {"start": v(0, 177.8) * mm, "end": v(160.78, 177.8) * mm, "construction": true});
            skFitSpline(sketch, "E292", {"points": [v(152.4, 183.39) * mm, v(160.78, 177.8) * mm, v(177.8, 165.6) * mm, v(194.56, 152.4) * mm, v(203.2, 145.54) * mm, v(224.03, 127) * mm, v(228.6, 122.17) * mm, v(243.59, 101.6) * mm, v(252.98, 76.2) * mm, v(254, 71.12) * mm, v(255.78, 50.8) * mm, v(254.76, 25.4) * mm, v(254, 18.29) * mm, v(251.2, 0) * mm, v(245.35, -22.48) * mm, v(228.6, -44.96) * mm, v(217.68, -50.8) * mm, v(203.2, -56.13) * mm, v(177.8, -62.74) * mm, v(152.4, -67.31) * mm, v(127, -71.37) * mm, v(101.6, -74.93) * mm, v(76.2, -78.49) * mm, v(50.8, -81.03) * mm, v(25.4, -83.57) * mm, v(0, -85.6) * mm], "startDerivative": vector(644.43, -402.06) * mm, "endDerivative": vector(-557.3, -41.16) * mm});
            skFitSpline(sketch, "E293.MirrorCS", {"points": [v(-152.4, 183.39) * mm, v(-160.78, 177.8) * mm, v(-177.8, 165.6) * mm, v(-194.56, 152.4) * mm, v(-203.2, 145.54) * mm, v(-224.03, 127) * mm, v(-228.6, 122.17) * mm, v(-243.59, 101.6) * mm, v(-252.98, 76.2) * mm, v(-254, 71.12) * mm, v(-255.78, 50.8) * mm, v(-254.76, 25.4) * mm, v(-254, 18.29) * mm, v(-251.2, 0) * mm, v(-245.35, -22.48) * mm, v(-228.6, -44.96) * mm, v(-217.68, -50.8) * mm, v(-203.2, -56.13) * mm, v(-177.8, -62.74) * mm, v(-152.4, -67.31) * mm, v(-127, -71.37) * mm, v(-101.6, -74.93) * mm, v(-76.2, -78.49) * mm, v(-50.8, -81.03) * mm, v(-25.4, -83.57) * mm, v(0, -85.6) * mm], "startDerivative": vector(-644.43, -402.06) * mm, "endDerivative": vector(557.3, -41.16) * mm});
            skPoint(sketch, "E294", {"position": v(25.4, 183.39) * mm});
            skPoint(sketch, "E295", {"position": v(50.8, 183.39) * mm});
            skPoint(sketch, "E296", {"position": v(76.2, 183.39) * mm});
            skPoint(sketch, "E297", {"position": v(127, 183.39) * mm});
            skPoint(sketch, "E298", {"position": v(101.6, 183.39) * mm});
            skPoint(sketch, "E299.MirrorP", {"position": v(-25.4, 183.39) * mm});
            skPoint(sketch, "E300.MirrorP", {"position": v(-50.8, 183.39) * mm});
            skPoint(sketch, "E301.MirrorP", {"position": v(-76.2, 183.39) * mm});
            skPoint(sketch, "E302.MirrorP", {"position": v(-101.6, 183.39) * mm});
            skPoint(sketch, "E303.MirrorP", {"position": v(-127, 183.39) * mm});
            skLineSegment(sketch, "E304", {"start": v(0, 0) * mm, "end": v(0, 183.39) * mm, "construction": true});
            skLineSegment(sketch, "E305", {"start": v(0, 183.39) * mm, "end": v(152.4, 183.39) * mm});
            skLineSegment(sketch, "E306.MirrorCS", {"start": v(0, 183.39) * mm, "end": v(-152.4, 183.39) * mm});
            skLineSegment(sketch, "E307", {"start": v(0, 183.39) * mm, "end": v(0, -85.6) * mm});
            skSolve(sketch);
        }
        {
            var Q0;
            Q0=makeQuery(id+"F16.imprint","IMPRINT",FACE,{"disambiguationData":[TD([[makeQuery(id+"F16.imprint","IMPRINT",EDGE,{"derivedFrom":sQuery(id+"F16.wireOp",EDGE,"E292")}),-1.0]])]});
            cPlane(context, id + "F17", {"entities" : qUnion([Q0]), "cplaneType" : CPlaneType.OFFSET, "offset" : 304.8 * mm, "oppositeDirection" : true, "width" : 152.4 * mm, "height" : 152.4 * mm});
        }
        {
            var Q0;
            Q0=qCreatedBy(id+"F17.planeOp",FACE);
            var sketch = newSketch(context, id + "F18", { "sketchPlane" : qUnion([Q0])});
            skPoint(sketch, "E308.0", {"position": v(0, -76.2) * mm});
            skPoint(sketch, "E309.0", {"position": v(0, -50.8) * mm});
            skPoint(sketch, "E310.0", {"position": v(0, -25.4) * mm});
            skPoint(sketch, "E311.0", {"position": v(0, 25.4) * mm});
            skPoint(sketch, "E312.0", {"position": v(0, 50.8) * mm});
            skPoint(sketch, "E313.0", {"position": v(0, 76.2) * mm});
            skPoint(sketch, "E314.0", {"position": v(0, 101.6) * mm});
            skPoint(sketch, "E315.0", {"position": v(0, 127) * mm});
            skPoint(sketch, "E316.0", {"position": v(0, 0) * mm});
            skPoint(sketch, "E317.0", {"position": v(25.4, 0) * mm});
            skPoint(sketch, "E318.0", {"position": v(50.8, 0) * mm});
            skPoint(sketch, "E319.0", {"position": v(76.2, 0) * mm});
            skPoint(sketch, "E320.0", {"position": v(101.6, 0) * mm});
            skPoint(sketch, "E321.0", {"position": v(127, 0) * mm});
            skPoint(sketch, "E322.0", {"position": v(152.4, 0) * mm});
            skPoint(sketch, "E323.0", {"position": v(177.8, 0) * mm});
            skPoint(sketch, "E324.0", {"position": v(203.2, 0) * mm});
            skPoint(sketch, "E325.0", {"position": v(228.6, 0) * mm});
            skPoint(sketch, "E326.0", {"position": v(254, 0) * mm});
            skLineSegment(sketch, "E327", {"start": v(0, 0) * mm, "end": v(0, -86.87) * mm, "construction": true});
            skLineSegment(sketch, "E328", {"start": v(25.4, 0) * mm, "end": v(25.4, -84.84) * mm, "construction": true});
            skLineSegment(sketch, "E329", {"start": v(50.8, 0) * mm, "end": v(50.8, -82.55) * mm, "construction": true});
            skLineSegment(sketch, "E330", {"start": v(76.2, 0) * mm, "end": v(76.2, -79.76) * mm, "construction": true});
            skLineSegment(sketch, "E331", {"start": v(101.6, 0) * mm, "end": v(101.6, -76.96) * mm, "construction": true});
            skLineSegment(sketch, "E332", {"start": v(127, 0) * mm, "end": v(127, -73.91) * mm, "construction": true});
            skLineSegment(sketch, "E333", {"start": v(152.4, 0) * mm, "end": v(152.4, -70.36) * mm, "construction": true});
            skLineSegment(sketch, "E334", {"start": v(177.8, 0) * mm, "end": v(177.8, -66.55) * mm, "construction": true});
            skLineSegment(sketch, "E335", {"start": v(203.2, 0) * mm, "end": v(203.2, -61.98) * mm, "construction": true});
            skLineSegment(sketch, "E336", {"start": v(228.6, 0) * mm, "end": v(228.6, -54.1) * mm, "construction": true});
            skLineSegment(sketch, "E337", {"start": v(0, 0) * mm, "end": v(257.56, 0) * mm, "construction": true});
            skLineSegment(sketch, "E338", {"start": v(0, -25.4) * mm, "end": v(252.72, -27.05) * mm, "construction": true});
            skPoint(sketch, "E338.endSnap0", {"position": v(228.6, -27.05) * mm});
            skLineSegment(sketch, "E339", {"start": v(0, 25.4) * mm, "end": v(260.34, 23.7) * mm, "construction": true});
            skLineSegment(sketch, "E340", {"start": v(0, 50.8) * mm, "end": v(261.36, 49.1) * mm, "construction": true});
            skLineSegment(sketch, "E341", {"start": v(0, 76.2) * mm, "end": v(257.3, 76.2) * mm, "construction": true});
            skLineSegment(sketch, "E342", {"start": v(0, 101.6) * mm, "end": v(246.37, 100) * mm, "construction": true});
            skLineSegment(sketch, "E343", {"start": v(0, 127) * mm, "end": v(219.71, 127) * mm, "construction": true});
            skLineSegment(sketch, "E344", {"start": v(228.6, 0) * mm, "end": v(229.38, 120.14) * mm, "construction": true});
            skLineSegment(sketch, "E345", {"start": v(203.2, 0) * mm, "end": v(204.07, 132.59) * mm, "construction": true});
            skLineSegment(sketch, "E346", {"start": v(0, -50.8) * mm, "end": v(235.46, -50.8) * mm, "construction": true});
            skFitSpline(sketch, "E347", {"points": [v(204.07, 132.59) * mm, v(219.71, 127) * mm, v(229.38, 120.14) * mm, v(246.37, 100) * mm, v(257.3, 76.2) * mm, v(261.36, 49.1) * mm, v(260.34, 23.7) * mm, v(257.56, 0) * mm, v(252.72, -27.05) * mm, v(235.46, -50.8) * mm, v(228.6, -54.1) * mm, v(203.2, -61.98) * mm, v(177.8, -66.55) * mm, v(152.4, -70.36) * mm, v(127, -73.91) * mm, v(101.6, -76.96) * mm, v(76.2, -79.76) * mm, v(50.8, -82.55) * mm, v(25.4, -84.84) * mm, v(0, -86.87) * mm], "startDerivative": vector(451.47, -84.76) * mm, "endDerivative": vector(-462.88, -36.47) * mm});
            skLineSegment(sketch, "E348", {"start": v(204.07, 132.59) * mm, "end": v(0, 133.92) * mm});
            skFitSpline(sketch, "E349.MirrorCS", {"points": [v(-204.07, 132.59) * mm, v(-219.71, 127) * mm, v(-229.38, 120.14) * mm, v(-246.37, 100) * mm, v(-257.3, 76.2) * mm, v(-261.36, 49.1) * mm, v(-260.34, 23.7) * mm, v(-257.56, 0) * mm, v(-252.72, -27.05) * mm, v(-235.46, -50.8) * mm, v(-228.6, -54.1) * mm, v(-203.2, -61.98) * mm, v(-177.8, -66.55) * mm, v(-152.4, -70.36) * mm, v(-127, -73.91) * mm, v(-101.6, -76.96) * mm, v(-76.2, -79.76) * mm, v(-50.8, -82.55) * mm, v(-25.4, -84.84) * mm, v(0, -86.87) * mm], "startDerivative": vector(-451.47, -84.76) * mm, "endDerivative": vector(462.88, -36.47) * mm});
            skLineSegment(sketch, "E350.MirrorCS", {"start": v(-204.07, 132.59) * mm, "end": v(0, 133.92) * mm});
            skLineSegment(sketch, "E351", {"start": v(0, 133.92) * mm, "end": v(-0.13, 153.42) * mm, "construction": true});
            skPoint(sketch, "E352", {"position": v(25.4, 133.75) * mm});
            skPoint(sketch, "E353", {"position": v(50.8, 133.59) * mm});
            skPoint(sketch, "E354", {"position": v(76.2, 133.59) * mm});
            skPoint(sketch, "E355", {"position": v(101.6, 133.25) * mm});
            skPoint(sketch, "E356.positionSnap0", {"position": v(123.19, 100.8) * mm});
            skPoint(sketch, "E357", {"position": v(152.4, 132.92) * mm});
            skPoint(sketch, "E358", {"position": v(177.8, 132.76) * mm});
            skPoint(sketch, "E359.MirrorP", {"position": v(-25.4, 133.75) * mm});
            skPoint(sketch, "E360.MirrorP", {"position": v(-50.8, 133.59) * mm});
            skPoint(sketch, "E361.MirrorP", {"position": v(-76.2, 133.59) * mm});
            skPoint(sketch, "E362.MirrorP", {"position": v(-101.6, 133.25) * mm});
            skPoint(sketch, "E363.MirrorP", {"position": v(-152.4, 132.92) * mm});
            skPoint(sketch, "E364.MirrorP", {"position": v(-177.8, 132.76) * mm});
            skPoint(sketch, "E365", {"position": v(127, 133.09) * mm});
            skPoint(sketch, "E366.MirrorP", {"position": v(-127, 133.09) * mm});
            skLineSegment(sketch, "E367", {"start": v(0, 0) * mm, "end": v(0, 133.92) * mm, "construction": true});
            skLineSegment(sketch, "E368", {"start": v(0, 133.92) * mm, "end": v(0, -86.87) * mm});
            skSolve(sketch);
        }
        {
            var Q0;
            Q0=makeQuery(id+"F18.imprint","IMPRINT",FACE,{"disambiguationData":[TD([[makeQuery(id+"F18.imprint","IMPRINT",EDGE,{"derivedFrom":sQuery(id+"F18.wireOp",EDGE,"E347")}),-1.0]])]});
            cPlane(context, id + "F19", {"entities" : qUnion([Q0]), "cplaneType" : CPlaneType.OFFSET, "offset" : 304.8 * mm, "oppositeDirection" : true, "width" : 152.4 * mm, "height" : 152.4 * mm});
        }
        {
            var Q0;
            Q0=qCreatedBy(id+"F19.planeOp",FACE);
            var sketch = newSketch(context, id + "F20", { "sketchPlane" : qUnion([Q0])});
            skPoint(sketch, "E369.0", {"position": v(0, -76.2) * mm});
            skPoint(sketch, "E370.0", {"position": v(0, -50.8) * mm});
            skPoint(sketch, "E371.0", {"position": v(0, -25.4) * mm});
            skPoint(sketch, "E372.0", {"position": v(0, 0) * mm});
            skPoint(sketch, "E373.0", {"position": v(0, 25.4) * mm});
            skPoint(sketch, "E374.0", {"position": v(0, 50.8) * mm});
            skPoint(sketch, "E375.0", {"position": v(0, 76.2) * mm});
            skPoint(sketch, "E376.0", {"position": v(0, 101.6) * mm});
            skPoint(sketch, "E377.0", {"position": v(25.4, 0) * mm});
            skPoint(sketch, "E378.0", {"position": v(50.8, 0) * mm});
            skPoint(sketch, "E379.0", {"position": v(76.2, 0) * mm});
            skPoint(sketch, "E380.0", {"position": v(101.6, 0) * mm});
            skPoint(sketch, "E381.0", {"position": v(127, 0) * mm});
            skPoint(sketch, "E382.0", {"position": v(152.4, 0) * mm});
            skPoint(sketch, "E383.0", {"position": v(177.8, 0) * mm});
            skPoint(sketch, "E384.0", {"position": v(203.2, 0) * mm});
            skPoint(sketch, "E385.0", {"position": v(228.6, 0) * mm});
            skPoint(sketch, "E386.0", {"position": v(254, 0) * mm});
            skLineSegment(sketch, "E387", {"start": v(0, 0) * mm, "end": v(255.52, 0) * mm, "construction": true});
            skLineSegment(sketch, "E388", {"start": v(0, -25.4) * mm, "end": v(250.95, -25.4) * mm, "construction": true});
            skLineSegment(sketch, "E389", {"start": v(0, -50.8) * mm, "end": v(236.47, -50.8) * mm, "construction": true});
            skLineSegment(sketch, "E390", {"start": v(0, -76.2) * mm, "end": v(99.82, -76.2) * mm, "construction": true});
            skLineSegment(sketch, "E391", {"start": v(0, 25.4) * mm, "end": v(258.57, 25.4) * mm, "construction": true});
            skLineSegment(sketch, "E392", {"start": v(0, 50.8) * mm, "end": v(259.59, 50.8) * mm, "construction": true});
            skLineSegment(sketch, "E393", {"start": v(0, 76.2) * mm, "end": v(254, 76.2) * mm, "construction": true});
            skLineSegment(sketch, "E394", {"start": v(0, 101.6) * mm, "end": v(238.25, 101.6) * mm, "construction": true});
            skLineSegment(sketch, "E395", {"start": v(0, 0) * mm, "end": v(0, -86.1) * mm, "construction": true});
            skLineSegment(sketch, "E396", {"start": v(25.4, 0) * mm, "end": v(25.4, -84.07) * mm, "construction": true});
            skLineSegment(sketch, "E397", {"start": v(50.8, 0) * mm, "end": v(50.8, -81.53) * mm, "construction": true});
            skLineSegment(sketch, "E398", {"start": v(76.2, 0) * mm, "end": v(76.2, -79) * mm, "construction": true});
            skLineSegment(sketch, "E399", {"start": v(101.6, 0) * mm, "end": v(101.6, -75.95) * mm, "construction": true});
            skLineSegment(sketch, "E400", {"start": v(127, 0) * mm, "end": v(127, -72.9) * mm, "construction": true});
            skLineSegment(sketch, "E401", {"start": v(152.4, 0) * mm, "end": v(152.4, -69.34) * mm, "construction": true});
            skLineSegment(sketch, "E402", {"start": v(177.8, 0) * mm, "end": v(177.8, -65.53) * mm, "construction": true});
            skLineSegment(sketch, "E403", {"start": v(203.2, 0) * mm, "end": v(203.2, -61.47) * mm, "construction": true});
            skLineSegment(sketch, "E404", {"start": v(228.6, 0) * mm, "end": v(228.6, -54.61) * mm, "construction": true});
            skLineSegment(sketch, "E405", {"start": v(254, 0) * mm, "end": v(254, -9.4) * mm, "construction": true});
            skLineSegment(sketch, "E406", {"start": v(228.6, 0) * mm, "end": v(228.6, 108.46) * mm, "construction": true});
            skLineSegment(sketch, "E407", {"start": v(203.2, 0) * mm, "end": v(203.2, 113.28) * mm, "construction": true});
            skFitSpline(sketch, "E408", {"points": [v(203.2, 113.28) * mm, v(228.6, 108.46) * mm, v(238.25, 101.6) * mm, v(254, 76.2) * mm, v(259.59, 50.8) * mm, v(258.57, 25.4) * mm, v(255.52, 0) * mm, v(254, -9.4) * mm, v(250.95, -25.4) * mm, v(236.47, -50.8) * mm, v(228.6, -54.61) * mm, v(203.2, -61.47) * mm, v(177.8, -65.53) * mm, v(152.4, -69.34) * mm, v(127, -72.9) * mm, v(101.6, -75.95) * mm, v(99.82, -76.2) * mm, v(76.2, -79) * mm, v(50.8, -81.53) * mm, v(25.4, -84.07) * mm, v(0, -86.1) * mm], "startDerivative": vector(819.3, -36.48) * mm, "endDerivative": vector(-457.64, -33.9) * mm});
            skLineSegment(sketch, "E409", {"start": v(203.2, 113.28) * mm, "end": v(0, 113.28) * mm});
            skFitSpline(sketch, "E410.MirrorCS", {"points": [v(-203.2, 113.28) * mm, v(-228.6, 108.46) * mm, v(-238.25, 101.6) * mm, v(-254, 76.2) * mm, v(-259.59, 50.8) * mm, v(-258.57, 25.4) * mm, v(-255.52, 0) * mm, v(-254, -9.4) * mm, v(-250.95, -25.4) * mm, v(-236.47, -50.8) * mm, v(-228.6, -54.61) * mm, v(-203.2, -61.47) * mm, v(-177.8, -65.53) * mm, v(-152.4, -69.34) * mm, v(-127, -72.9) * mm, v(-101.6, -75.95) * mm, v(-99.82, -76.2) * mm, v(-76.2, -79) * mm, v(-50.8, -81.53) * mm, v(-25.4, -84.07) * mm, v(0, -86.1) * mm], "startDerivative": vector(-819.3, -36.48) * mm, "endDerivative": vector(457.64, -33.9) * mm});
            skLineSegment(sketch, "E411.MirrorCS", {"start": v(-203.2, 113.28) * mm, "end": v(0, 113.28) * mm});
            skPoint(sketch, "E412", {"position": v(25.4, 113.28) * mm});
            skPoint(sketch, "E413", {"position": v(50.8, 113.28) * mm});
            skPoint(sketch, "E414", {"position": v(76.2, 113.28) * mm});
            skPoint(sketch, "E415", {"position": v(127, 113.28) * mm});
            skPoint(sketch, "E415.positionSnap0", {"position": v(101.6, 113.28) * mm});
            skPoint(sketch, "E416", {"position": v(152.4, 113.28) * mm});
            skPoint(sketch, "E417", {"position": v(177.8, 113.28) * mm});
            skPoint(sketch, "E418.MirrorP", {"position": v(-25.4, 113.28) * mm});
            skPoint(sketch, "E419.MirrorP", {"position": v(-50.8, 113.28) * mm});
            skPoint(sketch, "E420.MirrorP", {"position": v(-76.2, 113.28) * mm});
            skPoint(sketch, "E421.MirrorP", {"position": v(-101.6, 113.28) * mm});
            skPoint(sketch, "E422.MirrorP", {"position": v(-127, 113.28) * mm});
            skPoint(sketch, "E423.MirrorP", {"position": v(-152.4, 113.28) * mm});
            skPoint(sketch, "E424.MirrorP", {"position": v(-177.8, 113.28) * mm});
            skLineSegment(sketch, "E425", {"start": v(0, 0) * mm, "end": v(0, 113.28) * mm, "construction": true});
            skLineSegment(sketch, "E426", {"start": v(0, 113.28) * mm, "end": v(0, -86.1) * mm});
            skSolve(sketch);
        }
        {
            var Q0;
            Q0=qCreatedBy(id+"F19.planeOp",FACE);
            cPlane(context, id + "F21", {"entities" : qUnion([Q0]), "cplaneType" : CPlaneType.OFFSET, "offset" : 304.8 * mm, "oppositeDirection" : true, "width" : 152.4 * mm, "height" : 152.4 * mm});
        }
        {
            var Q0;
            Q0=qCreatedBy(id+"F21.planeOp",FACE);
            var sketch = newSketch(context, id + "F22", { "sketchPlane" : qUnion([Q0])});
            skPoint(sketch, "E427.0", {"position": v(0, 25.4) * mm});
            skPoint(sketch, "E428.0", {"position": v(0, 50.8) * mm});
            skPoint(sketch, "E429.0", {"position": v(0, 76.2) * mm});
            skPoint(sketch, "E430.0", {"position": v(0, 101.6) * mm});
            skPoint(sketch, "E431.0", {"position": v(0, 127) * mm});
            skPoint(sketch, "E432.0", {"position": v(25.4, 0) * mm});
            skPoint(sketch, "E433.0", {"position": v(50.8, 0) * mm});
            skPoint(sketch, "E434.0", {"position": v(76.2, 0) * mm});
            skPoint(sketch, "E435.0", {"position": v(101.6, 0) * mm});
            skPoint(sketch, "E436.0", {"position": v(127, 0) * mm});
            skPoint(sketch, "E437.0", {"position": v(152.4, 0) * mm});
            skPoint(sketch, "E438.0", {"position": v(203.2, 0) * mm});
            skPoint(sketch, "E439.0", {"position": v(228.6, 0) * mm});
            skPoint(sketch, "E440.0", {"position": v(254, 0) * mm});
            skPoint(sketch, "E441.0", {"position": v(0, 0) * mm});
            skPoint(sketch, "E442.0", {"position": v(177.8, 0) * mm});
            skPoint(sketch, "E443.0", {"position": v(0, -25.4) * mm});
            skPoint(sketch, "E444.0", {"position": v(0, -50.8) * mm});
            skPoint(sketch, "E445.0", {"position": v(0, -76.2) * mm});
            skLineSegment(sketch, "E446", {"start": v(0, 0) * mm, "end": v(0, 145.03) * mm, "construction": true});
            skLineSegment(sketch, "E447", {"start": v(25.4, 0) * mm, "end": v(25.4, 142.5) * mm, "construction": true});
            skLineSegment(sketch, "E448", {"start": v(50.8, 0) * mm, "end": v(50.8, 139.95) * mm, "construction": true});
            skLineSegment(sketch, "E449", {"start": v(76.2, 0) * mm, "end": v(76.2, 136.65) * mm, "construction": true});
            skLineSegment(sketch, "E450", {"start": v(101.6, 0) * mm, "end": v(101.6, 132.84) * mm, "construction": true});
            skLineSegment(sketch, "E451", {"start": v(127, 0) * mm, "end": v(127, 128.02) * mm, "construction": true});
            skLineSegment(sketch, "E452", {"start": v(152.4, 0) * mm, "end": v(152.4, 122.94) * mm, "construction": true});
            skLineSegment(sketch, "E453", {"start": v(177.8, 0) * mm, "end": v(177.8, 117.1) * mm, "construction": true});
            skLineSegment(sketch, "E454", {"start": v(203.2, 0) * mm, "end": v(203.2, 108.71) * mm, "construction": true});
            skLineSegment(sketch, "E455", {"start": v(228.6, 0) * mm, "end": v(228.6, 92.46) * mm, "construction": true});
            skLineSegment(sketch, "E456", {"start": v(0, 0) * mm, "end": v(0, -83.06) * mm, "construction": true});
            skLineSegment(sketch, "E457", {"start": v(25.4, 0) * mm, "end": v(25.4, -80.77) * mm, "construction": true});
            skLineSegment(sketch, "E458", {"start": v(50.8, 0) * mm, "end": v(50.8, -77.98) * mm, "construction": true});
            skLineSegment(sketch, "E459", {"start": v(76.2, 0) * mm, "end": v(76.2, -74.68) * mm, "construction": true});
            skLineSegment(sketch, "E460", {"start": v(101.6, 0) * mm, "end": v(101.6, -71.37) * mm, "construction": true});
            skLineSegment(sketch, "E461", {"start": v(127, 0) * mm, "end": v(127, -67.82) * mm, "construction": true});
            skLineSegment(sketch, "E462", {"start": v(152.4, 0) * mm, "end": v(152.4, -64) * mm, "construction": true});
            skLineSegment(sketch, "E463", {"start": v(177.8, 0) * mm, "end": v(177.8, -59.94) * mm, "construction": true});
            skLineSegment(sketch, "E464", {"start": v(203.2, 0) * mm, "end": v(203.2, -55.37) * mm, "construction": true});
            skLineSegment(sketch, "E465", {"start": v(228.6, 0) * mm, "end": v(228.6, -46.48) * mm, "construction": true});
            skLineSegment(sketch, "E466", {"start": v(0, 0) * mm, "end": v(244.35, 0) * mm, "construction": true});
            skLineSegment(sketch, "E467", {"start": v(0, -25.4) * mm, "end": v(239.01, -25.4) * mm, "construction": true});
            skLineSegment(sketch, "E468", {"start": v(0, 25.4) * mm, "end": v(247.9, 25.4) * mm, "construction": true});
            skLineSegment(sketch, "E469", {"start": v(0, 50.8) * mm, "end": v(249.17, 50.8) * mm, "construction": true});
            skLineSegment(sketch, "E470", {"start": v(0, 76.2) * mm, "end": v(241.3, 76.2) * mm, "construction": true});
            skLineSegment(sketch, "E471", {"start": v(0, 101.6) * mm, "end": v(216.4, 101.6) * mm, "construction": true});
            skFitSpline(sketch, "E472", {"points": [v(0, 145.03) * mm, v(25.4, 142.5) * mm, v(50.8, 139.95) * mm, v(76.2, 136.65) * mm, v(101.6, 132.84) * mm, v(127, 128.02) * mm, v(152.4, 122.94) * mm, v(177.8, 117.1) * mm, v(203.2, 108.71) * mm, v(216.4, 101.6) * mm, v(228.6, 92.46) * mm, v(241.3, 76.2) * mm, v(249.17, 50.8) * mm, v(247.9, 25.4) * mm, v(244.35, 0) * mm, v(239.01, -25.4) * mm, v(228.6, -46.48) * mm, v(203.2, -55.37) * mm, v(177.8, -59.94) * mm, v(152.4, -64) * mm, v(127, -67.82) * mm, v(101.6, -71.37) * mm, v(76.2, -74.68) * mm, v(50.8, -77.98) * mm, v(25.4, -80.77) * mm, v(0, -83.06) * mm], "startDerivative": vector(1143.06, -88.15) * mm, "endDerivative": vector(-623.34, -53.68) * mm});
            skFitSpline(sketch, "E473.MirrorCS", {"points": [v(0, 145.03) * mm, v(-25.4, 142.5) * mm, v(-50.8, 139.95) * mm, v(-76.2, 136.65) * mm, v(-101.6, 132.84) * mm, v(-127, 128.02) * mm, v(-152.4, 122.94) * mm, v(-177.8, 117.1) * mm, v(-203.2, 108.71) * mm, v(-216.4, 101.6) * mm, v(-228.6, 92.46) * mm, v(-241.3, 76.2) * mm, v(-249.17, 50.8) * mm, v(-247.9, 25.4) * mm, v(-244.35, 0) * mm, v(-239.01, -25.4) * mm, v(-228.6, -46.48) * mm, v(-203.2, -55.37) * mm, v(-177.8, -59.94) * mm, v(-152.4, -64) * mm, v(-127, -67.82) * mm, v(-101.6, -71.37) * mm, v(-76.2, -74.68) * mm, v(-50.8, -77.98) * mm, v(-25.4, -80.77) * mm, v(0, -83.06) * mm], "startDerivative": vector(-1143.06, -88.15) * mm, "endDerivative": vector(623.34, -53.68) * mm});
            skLineSegment(sketch, "E474", {"start": v(0, 145.03) * mm, "end": v(0, -83.06) * mm});
            skSolve(sketch);
        }
        {
            var Q0;
            Q0=qCreatedBy(id+"F21.planeOp",FACE);
            cPlane(context, id + "F23", {"entities" : qUnion([Q0]), "cplaneType" : CPlaneType.OFFSET, "offset" : 304.8 * mm, "oppositeDirection" : true, "width" : 152.4 * mm, "height" : 152.4 * mm});
        }
        {
            var Q0;
            Q0=qCreatedBy(id+"F23.planeOp",FACE);
            var sketch = newSketch(context, id + "F24", { "sketchPlane" : qUnion([Q0])});
            skPoint(sketch, "E475.0", {"position": v(0, 0) * mm});
            skPoint(sketch, "E475.1", {"position": v(25.4, 0) * mm});
            skPoint(sketch, "E475.2", {"position": v(50.8, 0) * mm});
            skPoint(sketch, "E475.3", {"position": v(76.2, 0) * mm});
            skPoint(sketch, "E475.4", {"position": v(101.6, 0) * mm});
            skPoint(sketch, "E475.5", {"position": v(127, 0) * mm});
            skPoint(sketch, "E475.6", {"position": v(152.4, 0) * mm});
            skPoint(sketch, "E475.7", {"position": v(177.8, 0) * mm});
            skPoint(sketch, "E475.8", {"position": v(203.2, 0) * mm});
            skPoint(sketch, "E475.9", {"position": v(228.6, 0) * mm});
            skPoint(sketch, "E475.12", {"position": v(0, 25.4) * mm});
            skPoint(sketch, "E475.13", {"position": v(0, 50.8) * mm});
            skPoint(sketch, "E475.14", {"position": v(0, 76.2) * mm});
            skPoint(sketch, "E475.15", {"position": v(0, 101.6) * mm});
            skPoint(sketch, "E475.16", {"position": v(0, 127) * mm});
            skLineSegment(sketch, "E476", {"start": v(0, 0) * mm, "end": v(0, -79) * mm, "construction": true});
            skLineSegment(sketch, "E477", {"start": v(25.4, 0) * mm, "end": v(25.4, -75.44) * mm, "construction": true});
            skLineSegment(sketch, "E478", {"start": v(50.8, 0) * mm, "end": v(50.8, -71.37) * mm, "construction": true});
            skLineSegment(sketch, "E479", {"start": v(76.2, 0) * mm, "end": v(76.2, -67.31) * mm, "construction": true});
            skLineSegment(sketch, "E480", {"start": v(101.6, 0) * mm, "end": v(101.6, -63.25) * mm, "construction": true});
            skLineSegment(sketch, "E481", {"start": v(127, 0) * mm, "end": v(127, -58.93) * mm, "construction": true});
            skLineSegment(sketch, "E482", {"start": v(152.4, 0) * mm, "end": v(152.4, -54.61) * mm, "construction": true});
            skLineSegment(sketch, "E483", {"start": v(177.8, 0) * mm, "end": v(177.8, -49.78) * mm, "construction": true});
            skLineSegment(sketch, "E484", {"start": v(203.2, 0) * mm, "end": v(203.2, -43.18) * mm, "construction": true});
            skLineSegment(sketch, "E485", {"start": v(228.6, 0) * mm, "end": v(228.6, 26.67) * mm, "construction": true});
            skLineSegment(sketch, "E486", {"start": v(0, 0) * mm, "end": v(0, 135.38) * mm, "construction": true});
            skLineSegment(sketch, "E487", {"start": v(25.4, 0) * mm, "end": v(25.4, 133.1) * mm, "construction": true});
            skLineSegment(sketch, "E488", {"start": v(50.8, 0) * mm, "end": v(50.8, 130.56) * mm, "construction": true});
            skLineSegment(sketch, "E489", {"start": v(76.2, 0) * mm, "end": v(76.2, 127.5) * mm, "construction": true});
            skLineSegment(sketch, "E490", {"start": v(101.6, 0) * mm, "end": v(101.6, 123.7) * mm, "construction": true});
            skLineSegment(sketch, "E491", {"start": v(127, 0) * mm, "end": v(127, 119.38) * mm, "construction": true});
            skLineSegment(sketch, "E492", {"start": v(152.4, 0) * mm, "end": v(152.4, 114.05) * mm, "construction": true});
            skLineSegment(sketch, "E493", {"start": v(177.8, 0) * mm, "end": v(177.8, 105.66) * mm, "construction": true});
            skLineSegment(sketch, "E494", {"start": v(203.2, 0) * mm, "end": v(203.2, 91.95) * mm, "construction": true});
            skLineSegment(sketch, "E495", {"start": v(228.6, 0) * mm, "end": v(228.6, 58.67) * mm, "construction": true});
            skLineSegment(sketch, "E496", {"start": v(0, 0) * mm, "end": v(224.03, 0) * mm, "construction": true});
            skLineSegment(sketch, "E497", {"start": v(224.03, 0) * mm, "end": v(228.6, 0) * mm, "construction": true});
            skLineSegment(sketch, "E498", {"start": v(0, 25.4) * mm, "end": v(228.35, 25.4) * mm, "construction": true});
            skLineSegment(sketch, "E499", {"start": v(0, 76.2) * mm, "end": v(220.47, 76.2) * mm, "construction": true});
            skPoint(sketch, "E500.0", {"position": v(0, -25.4) * mm});
            skPoint(sketch, "E501.0", {"position": v(0, -50.8) * mm});
            skPoint(sketch, "E502.0", {"position": v(0, -76.2) * mm});
            skLineSegment(sketch, "E503", {"start": v(0, -25.4) * mm, "end": v(217.93, -25.4) * mm, "construction": true});
            skFitSpline(sketch, "E504", {"points": [v(0, 135.38) * mm, v(25.4, 133.1) * mm, v(50.8, 130.56) * mm, v(76.2, 127.5) * mm, v(101.6, 123.7) * mm, v(127, 119.38) * mm, v(152.4, 114.05) * mm, v(177.8, 105.66) * mm, v(203.2, 91.95) * mm, v(220.47, 76.2) * mm, v(228.6, 58.67) * mm, v(228.6, 26.67) * mm, v(228.35, 25.4) * mm, v(224.03, 0) * mm, v(217.93, -25.4) * mm, v(203.2, -43.18) * mm, v(177.8, -49.78) * mm, v(152.4, -54.61) * mm, v(127, -58.93) * mm, v(101.6, -63.25) * mm, v(76.2, -67.31) * mm, v(50.8, -71.37) * mm, v(25.4, -75.44) * mm, v(0, -79) * mm], "startDerivative": vector(1027.8, -60.68) * mm, "endDerivative": vector(-575.97, -77.6) * mm});
            skFitSpline(sketch, "E505.MirrorCS", {"points": [v(0, 135.38) * mm, v(-25.4, 133.1) * mm, v(-50.8, 130.56) * mm, v(-76.2, 127.5) * mm, v(-101.6, 123.7) * mm, v(-127, 119.38) * mm, v(-152.4, 114.05) * mm, v(-177.8, 105.66) * mm, v(-203.2, 91.95) * mm, v(-220.47, 76.2) * mm, v(-228.6, 58.67) * mm, v(-228.6, 26.67) * mm, v(-228.35, 25.4) * mm, v(-224.03, 0) * mm, v(-217.93, -25.4) * mm, v(-203.2, -43.18) * mm, v(-177.8, -49.78) * mm, v(-152.4, -54.61) * mm, v(-127, -58.93) * mm, v(-101.6, -63.25) * mm, v(-76.2, -67.31) * mm, v(-50.8, -71.37) * mm, v(-25.4, -75.44) * mm, v(0, -79) * mm], "startDerivative": vector(-1027.8, -60.68) * mm, "endDerivative": vector(575.97, -77.6) * mm});
            skLineSegment(sketch, "E506", {"start": v(0, 135.38) * mm, "end": v(0, -79) * mm});
            skSolve(sketch);
        }
        {
            var Q0;
            Q0=makeQuery(id+"F24.imprint","IMPRINT",FACE,{"disambiguationData":[TD([[makeQuery(id+"F24.imprint","IMPRINT",EDGE,{"derivedFrom":sQuery(id+"F24.wireOp",EDGE,"E504")}),-1.0]])]});
            cPlane(context, id + "F25", {"entities" : qUnion([Q0]), "cplaneType" : CPlaneType.OFFSET, "offset" : 304.8 * mm, "oppositeDirection" : true, "width" : 152.4 * mm, "height" : 152.4 * mm});
        }
        {
            var Q0;
            Q0=qCreatedBy(id+"F25.planeOp",FACE);
            var sketch = newSketch(context, id + "F26", { "sketchPlane" : qUnion([Q0])});
            skPoint(sketch, "E507.0", {"position": v(0, -76.2) * mm});
            skPoint(sketch, "E507.1", {"position": v(0, -50.8) * mm});
            skPoint(sketch, "E507.2", {"position": v(0, -25.4) * mm});
            skPoint(sketch, "E507.3", {"position": v(0, 0) * mm});
            skPoint(sketch, "E507.4", {"position": v(0, 25.4) * mm});
            skPoint(sketch, "E507.5", {"position": v(0, 50.8) * mm});
            skPoint(sketch, "E507.6", {"position": v(0, 76.2) * mm});
            skPoint(sketch, "E507.7", {"position": v(0, 101.6) * mm});
            skPoint(sketch, "E507.8", {"position": v(0, 127) * mm});
            skPoint(sketch, "E507.11", {"position": v(25.4, 0) * mm});
            skPoint(sketch, "E507.12", {"position": v(50.8, 0) * mm});
            skPoint(sketch, "E507.13", {"position": v(76.2, 0) * mm});
            skPoint(sketch, "E507.14", {"position": v(101.6, 0) * mm});
            skPoint(sketch, "E507.15", {"position": v(127, 0) * mm});
            skPoint(sketch, "E507.16", {"position": v(152.4, 0) * mm});
            skPoint(sketch, "E507.17", {"position": v(177.8, 0) * mm});
            skPoint(sketch, "E507.18", {"position": v(203.2, 0) * mm});
            skLineSegment(sketch, "E508", {"start": v(0, 0) * mm, "end": v(0, 127) * mm, "construction": true});
            skLineSegment(sketch, "E509", {"start": v(25.4, 0) * mm, "end": v(25.4, 124.97) * mm, "construction": true});
            skLineSegment(sketch, "E510", {"start": v(50.8, 0) * mm, "end": v(50.8, 122.17) * mm, "construction": true});
            skLineSegment(sketch, "E511", {"start": v(76.2, 0) * mm, "end": v(76.2, 119.13) * mm, "construction": true});
            skLineSegment(sketch, "E512", {"start": v(101.6, 0) * mm, "end": v(101.6, 115.57) * mm, "construction": true});
            skLineSegment(sketch, "E513", {"start": v(127, 0) * mm, "end": v(127, 110.24) * mm, "construction": true});
            skLineSegment(sketch, "E514", {"start": v(152.4, 0) * mm, "end": v(152.4, 101.85) * mm, "construction": true});
            skLineSegment(sketch, "E515", {"start": v(177.8, 0) * mm, "end": v(177.8, 88.9) * mm, "construction": true});
            skLineSegment(sketch, "E516", {"start": v(0, 0) * mm, "end": v(0, -73.91) * mm, "construction": true});
            skLineSegment(sketch, "E517", {"start": v(50.8, 0) * mm, "end": v(50.8, -61.21) * mm, "construction": true});
            skLineSegment(sketch, "E518", {"start": v(25.4, 0) * mm, "end": v(25.4, -66.3) * mm, "construction": true});
            skLineSegment(sketch, "E519", {"start": v(76.2, 0) * mm, "end": v(76.2, -55.37) * mm, "construction": true});
            skLineSegment(sketch, "E520", {"start": v(101.6, 0) * mm, "end": v(101.6, -49.78) * mm, "construction": true});
            skLineSegment(sketch, "E521", {"start": v(127, 0) * mm, "end": v(127, -43.94) * mm, "construction": true});
            skLineSegment(sketch, "E522", {"start": v(152.4, 0) * mm, "end": v(152.4, -37.85) * mm, "construction": true});
            skLineSegment(sketch, "E523", {"start": v(0, 0) * mm, "end": v(191.52, 0) * mm, "construction": true});
            skLineSegment(sketch, "E524", {"start": v(0, -25.4) * mm, "end": v(180.34, -25.4) * mm, "construction": true});
            skLineSegment(sketch, "E525", {"start": v(0, 25.4) * mm, "end": v(198.12, 25.4) * mm, "construction": true});
            skLineSegment(sketch, "E526", {"start": v(0, 50.8) * mm, "end": v(201.68, 50.8) * mm, "construction": true});
            skLineSegment(sketch, "E527", {"start": v(0, 76.2) * mm, "end": v(192.02, 76.2) * mm, "construction": true});
            skFitSpline(sketch, "E528", {"points": [v(0, 127) * mm, v(25.4, 124.97) * mm, v(50.8, 122.17) * mm, v(76.2, 119.13) * mm, v(101.6, 115.57) * mm, v(127, 110.24) * mm, v(152.4, 101.85) * mm, v(177.8, 88.9) * mm, v(192.02, 76.2) * mm, v(201.68, 50.8) * mm, v(198.12, 25.4) * mm, v(191.52, 0) * mm, v(180.34, -25.4) * mm, v(152.4, -37.85) * mm, v(127, -43.94) * mm, v(101.6, -49.78) * mm, v(76.2, -55.37) * mm, v(50.8, -61.21) * mm, v(25.4, -66.3) * mm, v(0, -73.91) * mm], "startDerivative": vector(1028.84, -62.93) * mm, "endDerivative": vector(-484.74, -159.9) * mm});
            skFitSpline(sketch, "E529.MirrorCS", {"points": [v(0, 127) * mm, v(-25.4, 124.97) * mm, v(-50.8, 122.17) * mm, v(-76.2, 119.13) * mm, v(-101.6, 115.57) * mm, v(-127, 110.24) * mm, v(-152.4, 101.85) * mm, v(-177.8, 88.9) * mm, v(-192.02, 76.2) * mm, v(-201.68, 50.8) * mm, v(-198.12, 25.4) * mm, v(-191.52, 0) * mm, v(-180.34, -25.4) * mm, v(-152.4, -37.85) * mm, v(-127, -43.94) * mm, v(-101.6, -49.78) * mm, v(-76.2, -55.37) * mm, v(-50.8, -61.21) * mm, v(-25.4, -66.3) * mm, v(0, -73.91) * mm], "startDerivative": vector(-1028.84, -62.93) * mm, "endDerivative": vector(484.74, -159.9) * mm});
            skLineSegment(sketch, "E530", {"start": v(0, 127) * mm, "end": v(0, -73.91) * mm});
            skSolve(sketch);
        }
        {
            var Q0;
            Q0=qCreatedBy(id+"F25.planeOp",FACE);
            cPlane(context, id + "F27", {"entities" : qUnion([Q0]), "cplaneType" : CPlaneType.OFFSET, "offset" : 304.8 * mm, "oppositeDirection" : true, "width" : 152.4 * mm, "height" : 152.4 * mm});
        }
        {
            var Q0;
            Q0=qCreatedBy(id+"F27.planeOp",FACE);
            var sketch = newSketch(context, id + "F28", { "sketchPlane" : qUnion([Q0])});
            skPoint(sketch, "E531.0", {"position": v(0, 0) * mm});
            skPoint(sketch, "E531.1", {"position": v(25.4, 0) * mm});
            skPoint(sketch, "E531.2", {"position": v(50.8, 0) * mm});
            skPoint(sketch, "E531.3", {"position": v(76.2, 0) * mm});
            skPoint(sketch, "E531.4", {"position": v(101.6, 0) * mm});
            skPoint(sketch, "E531.5", {"position": v(127, 0) * mm});
            skPoint(sketch, "E531.6", {"position": v(152.4, 0) * mm});
            skPoint(sketch, "E531.10", {"position": v(0, -25.4) * mm});
            skPoint(sketch, "E531.11", {"position": v(0, -50.8) * mm});
            skPoint(sketch, "E531.12", {"position": v(0, 25.4) * mm});
            skPoint(sketch, "E531.13", {"position": v(0, 50.8) * mm});
            skPoint(sketch, "E531.14", {"position": v(0, 76.2) * mm});
            skPoint(sketch, "E531.15", {"position": v(0, 101.6) * mm});
            skLineSegment(sketch, "E532", {"start": v(0, 0) * mm, "end": v(0, 120.14) * mm, "construction": true});
            skLineSegment(sketch, "E533", {"start": v(25.4, 0) * mm, "end": v(25.4, 117.86) * mm, "construction": true});
            skLineSegment(sketch, "E534", {"start": v(50.8, 0) * mm, "end": v(50.8, 114.8) * mm, "construction": true});
            skLineSegment(sketch, "E535", {"start": v(76.2, 0) * mm, "end": v(76.2, 111) * mm, "construction": true});
            skLineSegment(sketch, "E536", {"start": v(101.6, 0) * mm, "end": v(101.6, 104.9) * mm, "construction": true});
            skLineSegment(sketch, "E537", {"start": v(127, 0) * mm, "end": v(127, 95.76) * mm, "construction": true});
            skLineSegment(sketch, "E538", {"start": v(152.4, 0) * mm, "end": v(152.4, 76.45) * mm, "construction": true});
            skLineSegment(sketch, "E539", {"start": v(0, 0) * mm, "end": v(0, -63) * mm, "construction": true});
            skLineSegment(sketch, "E540", {"start": v(25.4, 0) * mm, "end": v(25.4, -51.82) * mm, "construction": true});
            skLineSegment(sketch, "E541", {"start": v(50.8, 0) * mm, "end": v(50.8, -42.93) * mm, "construction": true});
            skLineSegment(sketch, "E542", {"start": v(76.2, 0) * mm, "end": v(76.2, -34.8) * mm, "construction": true});
            skLineSegment(sketch, "E543", {"start": v(101.6, 0) * mm, "end": v(101.6, -26.67) * mm, "construction": true});
            skLineSegment(sketch, "E544", {"start": v(127, 0) * mm, "end": v(127, -16.51) * mm, "construction": true});
            skLineSegment(sketch, "E545", {"start": v(152.4, 0) * mm, "end": v(152.4, 21.59) * mm, "construction": true});
            skLineSegment(sketch, "E546", {"start": v(0, 0) * mm, "end": v(143.26, 0) * mm, "construction": true});
            skLineSegment(sketch, "E547", {"start": v(0, -25.4) * mm, "end": v(105.66, -25.4) * mm, "construction": true});
            skLineSegment(sketch, "E548", {"start": v(0, 25.4) * mm, "end": v(153.67, 25.4) * mm, "construction": true});
            skLineSegment(sketch, "E549", {"start": v(0, 50.8) * mm, "end": v(160.02, 50.8) * mm, "construction": true});
            skFitSpline(sketch, "E550", {"points": [v(0, 120.14) * mm, v(25.4, 117.86) * mm, v(50.8, 114.8) * mm, v(76.2, 111) * mm, v(101.6, 104.9) * mm, v(127, 95.76) * mm, v(152.4, 76.45) * mm, v(160.02, 50.8) * mm, v(153.67, 25.4) * mm, v(152.4, 21.59) * mm, v(143.26, 0) * mm, v(127, -16.51) * mm, v(105.66, -25.4) * mm, v(101.6, -26.67) * mm, v(76.2, -34.8) * mm, v(50.8, -42.93) * mm, v(25.4, -51.82) * mm, v(0, -63) * mm], "startDerivative": vector(549.75, -20.4) * mm, "endDerivative": vector(-385.78, -178.7) * mm});
            skFitSpline(sketch, "E551.MirrorCS", {"points": [v(0, 120.14) * mm, v(-25.4, 117.86) * mm, v(-50.8, 114.8) * mm, v(-76.2, 111) * mm, v(-101.6, 104.9) * mm, v(-127, 95.76) * mm, v(-152.4, 76.45) * mm, v(-160.02, 50.8) * mm, v(-153.67, 25.4) * mm, v(-152.4, 21.59) * mm, v(-143.26, 0) * mm, v(-127, -16.51) * mm, v(-105.66, -25.4) * mm, v(-101.6, -26.67) * mm, v(-76.2, -34.8) * mm, v(-50.8, -42.93) * mm, v(-25.4, -51.82) * mm, v(0, -63) * mm], "startDerivative": vector(-549.75, -20.4) * mm, "endDerivative": vector(385.78, -178.7) * mm});
            skLineSegment(sketch, "E552", {"start": v(0, -63) * mm, "end": v(0, 120.14) * mm});
            skSolve(sketch);
        }
        {
            var Q0;
            Q0=qCreatedBy(id+"F27.planeOp",FACE);
            cPlane(context, id + "F29", {"entities" : qUnion([Q0]), "cplaneType" : CPlaneType.OFFSET, "offset" : 304.8 * mm, "oppositeDirection" : true, "width" : 152.4 * mm, "height" : 152.4 * mm});
        }
        {
            var Q0;
            Q0=qCreatedBy(id+"F29.planeOp",FACE);
            var sketch = newSketch(context, id + "F30", { "sketchPlane" : qUnion([Q0])});
            skPoint(sketch, "E553.0", {"position": v(0, 0) * mm});
            skPoint(sketch, "E554.0", {"position": v(0, 25.4) * mm});
            skPoint(sketch, "E555.0", {"position": v(0, 50.8) * mm});
            skPoint(sketch, "E556.0", {"position": v(0, 76.2) * mm});
            skPoint(sketch, "E557.0", {"position": v(0, 101.6) * mm});
            skPoint(sketch, "E558.0", {"position": v(25.4, 0) * mm});
            skPoint(sketch, "E559.0", {"position": v(50.8, 0) * mm});
            skPoint(sketch, "E560.0", {"position": v(76.2, 0) * mm});
            skPoint(sketch, "E561.0", {"position": v(101.6, 0) * mm});
            skPoint(sketch, "E562.0", {"position": v(0, -25.4) * mm});
            skLineSegment(sketch, "E563", {"start": v(0, 0) * mm, "end": v(0, 117.35) * mm, "construction": true});
            skLineSegment(sketch, "E564", {"start": v(25.4, 0) * mm, "end": v(25.4, 114.8) * mm, "construction": true});
            skLineSegment(sketch, "E565", {"start": v(50.8, 0) * mm, "end": v(50.8, 109.47) * mm, "construction": true});
            skLineSegment(sketch, "E566", {"start": v(76.2, 0) * mm, "end": v(76.2, 101.1) * mm, "construction": true});
            skLineSegment(sketch, "E567", {"start": v(0, 0) * mm, "end": v(0, -41.15) * mm, "construction": true});
            skLineSegment(sketch, "E568", {"start": v(25.4, 0) * mm, "end": v(25.4, -21.59) * mm, "construction": true});
            skLineSegment(sketch, "E569", {"start": v(50.8, 0) * mm, "end": v(50.8, -7.87) * mm, "construction": true});
            skLineSegment(sketch, "E570", {"start": v(76.2, 0) * mm, "end": v(76.2, 7.11) * mm, "construction": true});
            skLineSegment(sketch, "E571", {"start": v(101.6, 0) * mm, "end": v(101.6, 42.16) * mm, "construction": true});
            skLineSegment(sketch, "E572", {"start": v(0, 0) * mm, "end": v(65.02, 0) * mm, "construction": true});
            skLineSegment(sketch, "E573", {"start": v(0, 25.4) * mm, "end": v(92.96, 25.4) * mm, "construction": true});
            skLineSegment(sketch, "E574", {"start": v(0, 50.8) * mm, "end": v(104.9, 50.8) * mm, "construction": true});
            skLineSegment(sketch, "E575", {"start": v(0, 76.2) * mm, "end": v(106.17, 76.2) * mm, "construction": true});
            skLineSegment(sketch, "E576", {"start": v(0, -25.4) * mm, "end": v(19.3, -25.4) * mm, "construction": true});
            skFitSpline(sketch, "E577", {"points": [v(0, 117.35) * mm, v(25.4, 114.8) * mm, v(50.8, 109.47) * mm, v(76.2, 101.1) * mm, v(106.17, 76.2) * mm, v(104.9, 50.8) * mm, v(101.6, 42.16) * mm, v(92.96, 25.4) * mm, v(76.2, 7.11) * mm, v(65.02, 0) * mm, v(50.8, -7.87) * mm, v(25.4, -21.6) * mm, v(19.3, -25.4) * mm, v(0, -41.15) * mm], "startDerivative": vector(615.98, -53.26) * mm, "endDerivative": vector(-283.43, -236.5) * mm});
            skFitSpline(sketch, "E578.MirrorCS", {"points": [v(0, 117.35) * mm, v(-25.4, 114.8) * mm, v(-50.8, 109.47) * mm, v(-76.2, 101.1) * mm, v(-106.17, 76.2) * mm, v(-104.9, 50.8) * mm, v(-101.6, 42.16) * mm, v(-92.96, 25.4) * mm, v(-76.2, 7.11) * mm, v(-65.02, 0) * mm, v(-50.8, -7.87) * mm, v(-25.4, -21.6) * mm, v(-19.3, -25.4) * mm, v(0, -41.15) * mm], "startDerivative": vector(-615.98, -53.26) * mm, "endDerivative": vector(283.43, -236.5) * mm});
            skLineSegment(sketch, "E579", {"start": v(0, 117.35) * mm, "end": v(0, -41.15) * mm});
            skSolve(sketch);
        }
        {
            var Q0;
            Q0=makeQuery(id+"F30.imprint","IMPRINT",FACE,{"disambiguationData":[TD([[makeQuery(id+"F30.imprint","IMPRINT",EDGE,{"derivedFrom":sQuery(id+"F30.wireOp",EDGE,"E577")}),-1.0]])]});
            cPlane(context, id + "F31", {"entities" : qUnion([Q0]), "cplaneType" : CPlaneType.OFFSET, "offset" : 304.8 * mm, "oppositeDirection" : true, "width" : 152.4 * mm, "height" : 152.4 * mm});
        }
        {
            var Q0;
            Q0=qCreatedBy(id+"F31.planeOp",FACE);
            var sketch = newSketch(context, id + "F32", { "sketchPlane" : qUnion([Q0])});
            skPoint(sketch, "E580.0", {"position": v(0, 0) * mm});
            skPoint(sketch, "E581.0", {"position": v(0, 25.4) * mm});
            skPoint(sketch, "E582.0", {"position": v(0, 50.8) * mm});
            skPoint(sketch, "E583.0", {"position": v(0, 76.2) * mm});
            skPoint(sketch, "E584.0", {"position": v(25.4, 0) * mm});
            skPoint(sketch, "E585.0", {"position": v(50.8, 0) * mm});
            skPoint(sketch, "E586.0", {"position": v(0, 127) * mm});
            skPoint(sketch, "E587.0", {"position": v(0, 101.6) * mm});
            skLineSegment(sketch, "E588", {"start": v(0, 0) * mm, "end": v(0, 133.35) * mm, "construction": true});
            skLineSegment(sketch, "E589", {"start": v(25.4, 0) * mm, "end": v(25.4, 126.24) * mm, "construction": true});
            skLineSegment(sketch, "E590", {"start": v(50.8, 0) * mm, "end": v(50.8, 104.9) * mm, "construction": true});
            skLineSegment(sketch, "E591", {"start": v(0, 0) * mm, "end": v(0, 21.08) * mm, "construction": true});
            skLineSegment(sketch, "E592", {"start": v(25.4, 0) * mm, "end": v(25.4, 53.6) * mm, "construction": true});
            skLineSegment(sketch, "E593", {"start": v(50.8, 0) * mm, "end": v(50.8, 92.7) * mm, "construction": true});
            skLineSegment(sketch, "E594", {"start": v(0, 25.4) * mm, "end": v(2.03, 25.4) * mm, "construction": true});
            skLineSegment(sketch, "E595", {"start": v(0, 50.8) * mm, "end": v(22.6, 50.8) * mm, "construction": true});
            skLineSegment(sketch, "E596", {"start": v(0, 76.2) * mm, "end": v(43.18, 76.2) * mm, "construction": true});
            skLineSegment(sketch, "E597", {"start": v(0, 127) * mm, "end": v(23.62, 127) * mm, "construction": true});
            skFitSpline(sketch, "E598", {"points": [v(0, 133.35) * mm, v(23.62, 127) * mm, v(25.4, 126.24) * mm, v(50.8, 104.9) * mm, v(43.18, 76.2) * mm, v(22.6, 50.8) * mm, v(2.03, 25.4) * mm, v(0, 21.08) * mm], "startDerivative": vector(314.43, -71.84) * mm, "endDerivative": vector(-17.6, -51.72) * mm});
            skFitSpline(sketch, "E599.MirrorCS", {"points": [v(0, 133.35) * mm, v(-23.62, 127) * mm, v(-25.4, 126.24) * mm, v(-50.8, 104.9) * mm, v(-43.18, 76.2) * mm, v(-22.6, 50.8) * mm, v(-2.03, 25.4) * mm, v(0, 21.08) * mm], "startDerivative": vector(-314.43, -71.84) * mm, "endDerivative": vector(17.6, -51.72) * mm});
            skLineSegment(sketch, "E600", {"start": v(0, 133.35) * mm, "end": v(0, 21.08) * mm});
            skSolve(sketch);
        }
        {
            var Q0;
            Q0=makeQuery(id+"F32.imprint","IMPRINT",FACE,{"disambiguationData":[TD([[makeQuery(id+"F32.imprint","IMPRINT",EDGE,{"derivedFrom":sQuery(id+"F32.wireOp",EDGE,"E598")}),-1.0]])]});
            cPlane(context, id + "F33", {"entities" : qUnion([Q0]), "cplaneType" : CPlaneType.OFFSET, "offset" : 152.4 * mm, "oppositeDirection" : true, "width" : 152.4 * mm, "height" : 152.4 * mm});
        }
        {
            var Q0;
            Q0=qCreatedBy(id+"F33.planeOp",FACE);
            var sketch = newSketch(context, id + "F34", { "sketchPlane" : qUnion([Q0])});
            skPoint(sketch, "E601.0", {"position": v(0, 0) * mm});
            skPoint(sketch, "E602.0", {"position": v(0, 25.4) * mm});
            skPoint(sketch, "E603.0", {"position": v(0, 50.8) * mm});
            skPoint(sketch, "E604.0", {"position": v(0, 76.2) * mm});
            skPoint(sketch, "E605.0", {"position": v(0, 101.6) * mm});
            skPoint(sketch, "E606.0", {"position": v(0, 127) * mm});
            skPoint(sketch, "E607.0", {"position": v(0, 152.4) * mm});
            skLineSegment(sketch, "E608", {"start": v(0, 0) * mm, "end": v(0, 152.15) * mm, "construction": true});
            skLineSegment(sketch, "E609", {"start": v(0, 101.6) * mm, "end": v(11.18, 101.6) * mm, "construction": true});
            skLineSegment(sketch, "E610", {"start": v(0, 0) * mm, "end": v(0, 84.33) * mm, "construction": true});
            skLineSegment(sketch, "E611", {"start": v(0, 127) * mm, "end": v(22.86, 127) * mm, "construction": true});
            skFitSpline(sketch, "E612", {"points": [v(0, 152.15) * mm, v(22.86, 127) * mm, v(11.18, 101.6) * mm, v(0, 84.33) * mm], "startDerivative": vector(171.67, -54.13) * mm, "endDerivative": vector(-52.63, -105.12) * mm});
            skFitSpline(sketch, "E613.MirrorCS", {"points": [v(0, 152.15) * mm, v(-22.86, 127) * mm, v(-11.18, 101.6) * mm, v(0, 84.33) * mm], "startDerivative": vector(-171.67, -54.13) * mm, "endDerivative": vector(52.63, -105.12) * mm});
            skLineSegment(sketch, "E614", {"start": v(0, 152.4) * mm, "end": v(0, 84.33) * mm});
            skSolve(sketch);
        }
        {
            var Q0;
            Q0=qCreatedBy(makeId("Right.planeOp"),FACE);
            var sketch = newSketch(context, id + "F35", { "sketchPlane" : qUnion([Q0])});
            skPoint(sketch, "E615.0", {"position": v(-1981.2, 148.6) * mm});
            skPoint(sketch, "E616.0", {"position": v(-1828.8, 70.61) * mm});
            skPoint(sketch, "E617.0", {"position": v(-1524, -10.41) * mm});
            skPoint(sketch, "E618.0", {"position": v(-1219.2, -44.2) * mm});
            skPoint(sketch, "E619.0", {"position": v(-914.4, -61.47) * mm});
            skPoint(sketch, "E620.0", {"position": v(-609.6, -72.14) * mm});
            skPoint(sketch, "E621.0", {"position": v(-304.8, -78.23) * mm});
            skPoint(sketch, "E622.0", {"position": v(0, -82.55) * mm});
            skPoint(sketch, "E623.0", {"position": v(304.8, -85.6) * mm});
            skPoint(sketch, "E624.0", {"position": v(609.6, -86.87) * mm});
            skPoint(sketch, "E625.0", {"position": v(914.4, -86.1) * mm});
            skPoint(sketch, "E626.0", {"position": v(1219.2, -83.06) * mm});
            skPoint(sketch, "E627.0", {"position": v(1524, -79) * mm});
            skPoint(sketch, "E628.0", {"position": v(1828.8, -73.91) * mm});
            skPoint(sketch, "E629.0", {"position": v(2133.6, -63) * mm});
            skPoint(sketch, "E630.0", {"position": v(2438.4, -41.15) * mm});
            skPoint(sketch, "E631.0", {"position": v(2743.2, 21.08) * mm});
            skPoint(sketch, "E632.0", {"position": v(2895.6, 84.33) * mm});
            skFitSpline(sketch, "E633", {"points": [v(-1981.2, 148.6) * mm, v(-1828.8, 70.61) * mm, v(-1524, -10.41) * mm, v(-1219.2, -44.2) * mm, v(-914.4, -61.47) * mm, v(-609.6, -72.14) * mm, v(-304.8, -78.23) * mm, v(0, -82.55) * mm, v(304.8, -85.6) * mm, v(609.6, -86.87) * mm, v(914.4, -86.1) * mm, v(1219.2, -83.06) * mm, v(1524, -79) * mm, v(1828.8, -73.91) * mm, v(2133.6, -63) * mm, v(2438.4, -41.15) * mm, v(2743.2, 21.08) * mm, v(2895.6, 84.33) * mm], "startDerivative": vector(2997.54, -1768.44) * mm, "endDerivative": vector(3067.3, 1474.06) * mm});
            skPoint(sketch, "E634.0", {"position": v(2743.2, 133.35) * mm});
            skPoint(sketch, "E635.0", {"position": v(2438.4, 117.35) * mm});
            skPoint(sketch, "E636.0", {"position": v(2133.6, 120.14) * mm});
            skPoint(sketch, "E637.0", {"position": v(1828.8, 127) * mm});
            skPoint(sketch, "E638.0", {"position": v(1524, 135.38) * mm});
            skPoint(sketch, "E639.0", {"position": v(1219.2, 145.03) * mm});
            skPoint(sketch, "E640.0", {"position": v(609.6, 133.92) * mm});
            skPoint(sketch, "E641.0", {"position": v(0, 215.9) * mm});
            skPoint(sketch, "E642.0", {"position": v(-304.8, 198.12) * mm});
            skPoint(sketch, "E643.0", {"position": v(-609.6, 181.36) * mm});
            skPoint(sketch, "E644.0", {"position": v(-914.4, 168.15) * mm});
            skPoint(sketch, "E645.0", {"position": v(-1219.2, 161.3) * mm});
            skPoint(sketch, "E646.0", {"position": v(-1524, 163.58) * mm});
            skPoint(sketch, "E647.0", {"position": v(-1828.8, 195.07) * mm});
            skPoint(sketch, "E648.0", {"position": v(-1981.2, 227.33) * mm});
            skPoint(sketch, "E649.0", {"position": v(2895.6, 152.15) * mm});
            skPoint(sketch, "E650.0", {"position": v(304.8, 183.39) * mm});
            skPoint(sketch, "E651.0", {"position": v(914.4, 113.28) * mm});
            skFitSpline(sketch, "E652", {"points": [v(-1981.2, 227.33) * mm, v(-1828.8, 195.07) * mm, v(-1524, 163.58) * mm, v(-1219.2, 161.3) * mm, v(-914.4, 168.15) * mm, v(-609.6, 181.36) * mm, v(-304.8, 198.12) * mm, v(0, 215.9) * mm, v(12.39, 215.9) * mm, v(23.76, 215.9) * mm, v(152.1, 198.12) * mm, v(304.8, 183.39) * mm, v(415.32, 168.15) * mm, v(609.6, 133.92) * mm, v(745.33, 117.45) * mm, v(914.4, 113.28) * mm, v(1101.65, 113.28) * mm, v(1155.87, 113.28) * mm, v(1180.1, 121.8) * mm, v(1188.5, 133.92) * mm, v(1193.56, 142.42) * mm, v(1219.2, 145.03) * mm, v(1524, 135.38) * mm, v(1828.8, 127) * mm, v(2133.6, 120.14) * mm, v(2438.4, 117.35) * mm, v(2743.2, 133.35) * mm, v(2895.6, 152.15) * mm], "startDerivative": vector(3718.52, -898.53) * mm, "endDerivative": vector(3750.24, 535.8) * mm});
            skSolve(sketch);
        }
        {
            var Q0;
            {var subQ0=sQuery(id+"F34.wireOp",EDGE,"E613.MirrorCS");Q0=makeQuery(id+"F34.imprint","IMPRINT",FACE,{"disambiguationData":[TD([[makeQuery(id+"F34.imprint","IMPRINT",EDGE,{"derivedFrom":subQ0}),1.0]])]});}
            var Q1;
            Q1=makeQuery(id+"F32.imprint","IMPRINT",FACE,{"disambiguationData":[TD([[makeQuery(id+"F32.imprint","IMPRINT",EDGE,{"derivedFrom":sQuery(id+"F32.wireOp",EDGE,"E599.MirrorCS")}),1.0]])]});
            var Q2;
            Q2=makeQuery(id+"F30.imprint","IMPRINT",FACE,{"disambiguationData":[TD([[makeQuery(id+"F30.imprint","IMPRINT",EDGE,{"derivedFrom":sQuery(id+"F30.wireOp",EDGE,"E578.MirrorCS")}),1.0]])]});
            var Q3;
            Q3=makeQuery(id+"F28.imprint","IMPRINT",FACE,{"disambiguationData":[TD([[makeQuery(id+"F28.imprint","IMPRINT",EDGE,{"derivedFrom":sQuery(id+"F28.wireOp",EDGE,"E551.MirrorCS")}),1.0]])]});
            var Q4;
            Q4=makeQuery(id+"F26.imprint","IMPRINT",FACE,{"disambiguationData":[TD([[makeQuery(id+"F26.imprint","IMPRINT",EDGE,{"derivedFrom":sQuery(id+"F26.wireOp",EDGE,"E529.MirrorCS")}),1.0]])]});
            var Q5;
            Q5=makeQuery(id+"F24.imprint","IMPRINT",FACE,{"disambiguationData":[TD([[makeQuery(id+"F24.imprint","IMPRINT",EDGE,{"derivedFrom":sQuery(id+"F24.wireOp",EDGE,"E505.MirrorCS")}),1.0]])]});
            var Q6;
            Q6=makeQuery(id+"F22.imprint","IMPRINT",FACE,{"disambiguationData":[TD([[makeQuery(id+"F22.imprint","IMPRINT",EDGE,{"derivedFrom":sQuery(id+"F22.wireOp",EDGE,"E473.MirrorCS")}),1.0]])]});
            var Q7;
            Q7=makeQuery(id+"F20.imprint","IMPRINT",FACE,{"disambiguationData":[TD([[makeQuery(id+"F20.imprint","IMPRINT",EDGE,{"derivedFrom":sQuery(id+"F20.wireOp",EDGE,"E410.MirrorCS")}),1.0]])]});
            var Q8;
            Q8=makeQuery(id+"F18.imprint","IMPRINT",FACE,{"disambiguationData":[TD([[makeQuery(id+"F18.imprint","IMPRINT",EDGE,{"derivedFrom":sQuery(id+"F18.wireOp",EDGE,"E349.MirrorCS")}),1.0]])]});
            var Q9;
            Q9=makeQuery(id+"F16.imprint","IMPRINT",FACE,{"disambiguationData":[TD([[makeQuery(id+"F16.imprint","IMPRINT",EDGE,{"derivedFrom":sQuery(id+"F16.wireOp",EDGE,"E293.MirrorCS")}),1.0]])]});
            var Q10;
            Q10=makeQuery(id+"F0.imprint","IMPRINT",FACE,{"disambiguationData":[TD([[makeQuery(id+"F0.imprint","IMPRINT",EDGE,{"derivedFrom":sQuery(id+"F0.wireOp",EDGE,"E30.MirrorCS")}),1.0]])]});
            var Q11;
            Q11=makeQuery(id+"F2.imprint","IMPRINT",FACE,{"disambiguationData":[TD([[makeQuery(id+"F2.imprint","IMPRINT",EDGE,{"derivedFrom":sQuery(id+"F2.wireOp",EDGE,"E78.MirrorCS")}),1.0]])]});
            var Q12;
            Q12=makeQuery(id+"F4.imprint","IMPRINT",FACE,{"disambiguationData":[TD([[makeQuery(id+"F4.imprint","IMPRINT",EDGE,{"derivedFrom":sQuery(id+"F4.wireOp",EDGE,"E114.MirrorCS")}),1.0]])]});
            var Q13;
            Q13=makeQuery(id+"F6.imprint","IMPRINT",FACE,{"disambiguationData":[TD([[makeQuery(id+"F6.imprint","IMPRINT",EDGE,{"derivedFrom":sQuery(id+"F6.wireOp",EDGE,"E149.MirrorCS")}),1.0]])]});
            var Q14;
            Q14=makeQuery(id+"F8.imprint","IMPRINT",FACE,{"disambiguationData":[TD([[makeQuery(id+"F8.imprint","IMPRINT",EDGE,{"derivedFrom":sQuery(id+"F8.wireOp",EDGE,"E179.MirrorCS")}),1.0]])]});
            var Q15;
            Q15=makeQuery(id+"F10.imprint","IMPRINT",FACE,{"disambiguationData":[TD([[makeQuery(id+"F10.imprint","IMPRINT",EDGE,{"derivedFrom":sQuery(id+"F10.wireOp",EDGE,"E206.MirrorCS")}),1.0]])]});
            var Q16;
            Q16=makeQuery(id+"F12.imprint","IMPRINT",FACE,{"disambiguationData":[TD([[makeQuery(id+"F12.imprint","IMPRINT",EDGE,{"derivedFrom":sQuery(id+"F12.wireOp",EDGE,"E226.MirrorCS")}),1.0]])]});
            var Q17;
            Q17=makeQuery(id+"F14.imprint","IMPRINT",FACE,{"disambiguationData":[TD([[makeQuery(id+"F14.imprint","IMPRINT",EDGE,{"derivedFrom":sQuery(id+"F14.wireOp",EDGE,"E243.MirrorCS")}),1.0]])]});
            var Q18;
            Q18=sQuery(id+"F35.wireOp",EDGE,"E652");
            var Q19;
            Q19=sQuery(id+"F35.wireOp",EDGE,"E633");
            var Q20;
            Q20=sQuery(id+"F34.wireOp",VERTEX,"E613.MirrorCS.1.internal");
            var Q21;
            Q21=sQuery(id+"F32.wireOp",VERTEX,"E599.MirrorCS.3.internal");
            var Q22;
            Q22=sQuery(id+"F30.wireOp",VERTEX,"E578.MirrorCS.4.internal");
            var Q23;
            Q23=sQuery(id+"F28.wireOp",VERTEX,"E551.MirrorCS.6.internal");
            var Q24;
            Q24=sQuery(id+"F14.wireOp",VERTEX,"E243.MirrorCS.1.internal");
            var Q25;
            Q25=sQuery(id+"F18.wireOp",VERTEX,"E349.MirrorCS.3.internal");
            var Q26;
            Q26=sQuery(id+"F4.wireOp",VERTEX,"E114.MirrorCS.7.internal");
            var Q27;
            Q27=sQuery(id+"F6.wireOp",VERTEX,"E149.MirrorCS.6.internal");
            var Q28;
            Q28=sQuery(id+"F8.wireOp",VERTEX,"E179.MirrorCS.5.internal");
            var Q29;
            Q29=sQuery(id+"F10.wireOp",VERTEX,"E206.MirrorCS.5.internal");
            var Q30;
            Q30=sQuery(id+"F12.wireOp",VERTEX,"E226.MirrorCS.2.internal");
            var Q31;
            Q31=sQuery(id+"F20.wireOp",VERTEX,"E410.MirrorCS.3.internal");
            var Q32;
            Q32=sQuery(id+"F16.wireOp",VERTEX,"E293.MirrorCS.6.internal");
            var Q33;
            Q33=sQuery(id+"F22.wireOp",VERTEX,"E473.MirrorCS.11.internal");
            var Q34;
            Q34=sQuery(id+"F24.wireOp",VERTEX,"E505.MirrorCS.9.internal");
            var Q35;
            Q35=sQuery(id+"F2.wireOp",VERTEX,"E78.MirrorCS.7.internal");
            var Q36;
            Q36=sQuery(id+"F0.wireOp",VERTEX,"E30.MirrorCS.8.internal");
            var Q37;
            Q37=sQuery(id+"F26.wireOp",VERTEX,"E529.MirrorCS.8.internal");
            loft(context, id + "F36", {"addGuides" : true, "sheetProfilesArray" : [{ "sheetProfileEntities" : qUnion([Q0]) }, { "sheetProfileEntities" : qUnion([Q1]) }, { "sheetProfileEntities" : qUnion([Q2]) }, { "sheetProfileEntities" : qUnion([Q3]) }, { "sheetProfileEntities" : qUnion([Q4]) }, { "sheetProfileEntities" : qUnion([Q5]) }, { "sheetProfileEntities" : qUnion([Q6]) }, { "sheetProfileEntities" : qUnion([Q7]) }, { "sheetProfileEntities" : qUnion([Q8]) }, { "sheetProfileEntities" : qUnion([Q9]) }, { "sheetProfileEntities" : qUnion([Q10]) }, { "sheetProfileEntities" : qUnion([Q11]) }, { "sheetProfileEntities" : qUnion([Q12]) }, { "sheetProfileEntities" : qUnion([Q13]) }, { "sheetProfileEntities" : qUnion([Q14]) }, { "sheetProfileEntities" : qUnion([Q15]) }, { "sheetProfileEntities" : qUnion([Q16]) }, { "sheetProfileEntities" : qUnion([Q17]) }], "guidesArray" : [{ "guideEntities" : qUnion([Q18]), "guideDerivativeType" : LoftGuideDerivativeType.DEFAULT, "guideDerivativeMagnitude" : 1 }, { "guideEntities" : qUnion([Q19]), "guideDerivativeType" : LoftGuideDerivativeType.DEFAULT, "guideDerivativeMagnitude" : 1 }], "matchConnections" : true, "connections" : [{ "connectionEntities" : qUnion([Q20, Q21, Q22, Q23, Q24, Q25, Q26, Q27, Q28, Q29, Q30, Q31, Q32, Q33, Q34, Q35, Q36, Q37]), "connectionEdgeQueries" : qUnion([]), "connectionEdgeParameters" : [] }]});
        }
        {
            var Q0;
            {var subQ0=sQuery(id+"F34.wireOp",EDGE,"E613.MirrorCS");Q0=makeQuery(id+"F36.opLoft","SWEPT_BODY",BODY,{"disambiguationData":[OSD([sQuery(id+"F0.wireOp",EDGE,"E40"),sQuery(id+"F2.wireOp",EDGE,"E79"),sQuery(id+"F4.wireOp",EDGE,"E115"),sQuery(id+"F6.wireOp",EDGE,"E150"),sQuery(id+"F8.wireOp",EDGE,"E180"),sQuery(id+"F10.wireOp",EDGE,"E207"),sQuery(id+"F12.wireOp",EDGE,"E227"),makeQuery(id+"F14.imprint","IMPRINT",FACE,{"disambiguationData":[TD([[makeQuery(id+"F14.imprint","IMPRINT",EDGE,{"derivedFrom":sQuery(id+"F14.wireOp",EDGE,"E243.MirrorCS")}),1.0]])]}),sQuery(id+"F16.wireOp",EDGE,"E306.MirrorCS"),sQuery(id+"F18.wireOp",EDGE,"E350.MirrorCS"),sQuery(id+"F20.wireOp",EDGE,"E411.MirrorCS"),sQuery(id+"F22.wireOp",EDGE,"E474"),sQuery(id+"F24.wireOp",EDGE,"E506"),sQuery(id+"F26.wireOp",EDGE,"E530"),sQuery(id+"F28.wireOp",EDGE,"E551.MirrorCS"),sQuery(id+"F30.wireOp",EDGE,"E579"),sQuery(id+"F32.wireOp",EDGE,"E600"),makeQuery(id+"F34.imprint","IMPRINT",FACE,{"disambiguationData":[TD([[makeQuery(id+"F34.imprint","IMPRINT",EDGE,{"derivedFrom":subQ0}),1.0]])]}),sQuery(id+"F35.wireOp",EDGE,"E633"),sQuery(id+"F35.wireOp",EDGE,"E652")])]});}
            var Q1;
            Q1=makeQuery(id+"F36.opLoft","SWEPT_FACE",FACE,{"disambiguationData":[OSD([sQuery(id+"F32.wireOp",EDGE,"E600"),sQuery(id+"F34.wireOp",EDGE,"E614"),sQuery(id+"F35.wireOp",EDGE,"E633"),sQuery(id+"F35.wireOp",EDGE,"E652")])]});
            mirror(context, id + "F37", {"operationType" : NewBodyOperationType.ADD, "entities" : qUnion([Q0]), "mirrorPlane" : qUnion([Q1])});
        }
    });
